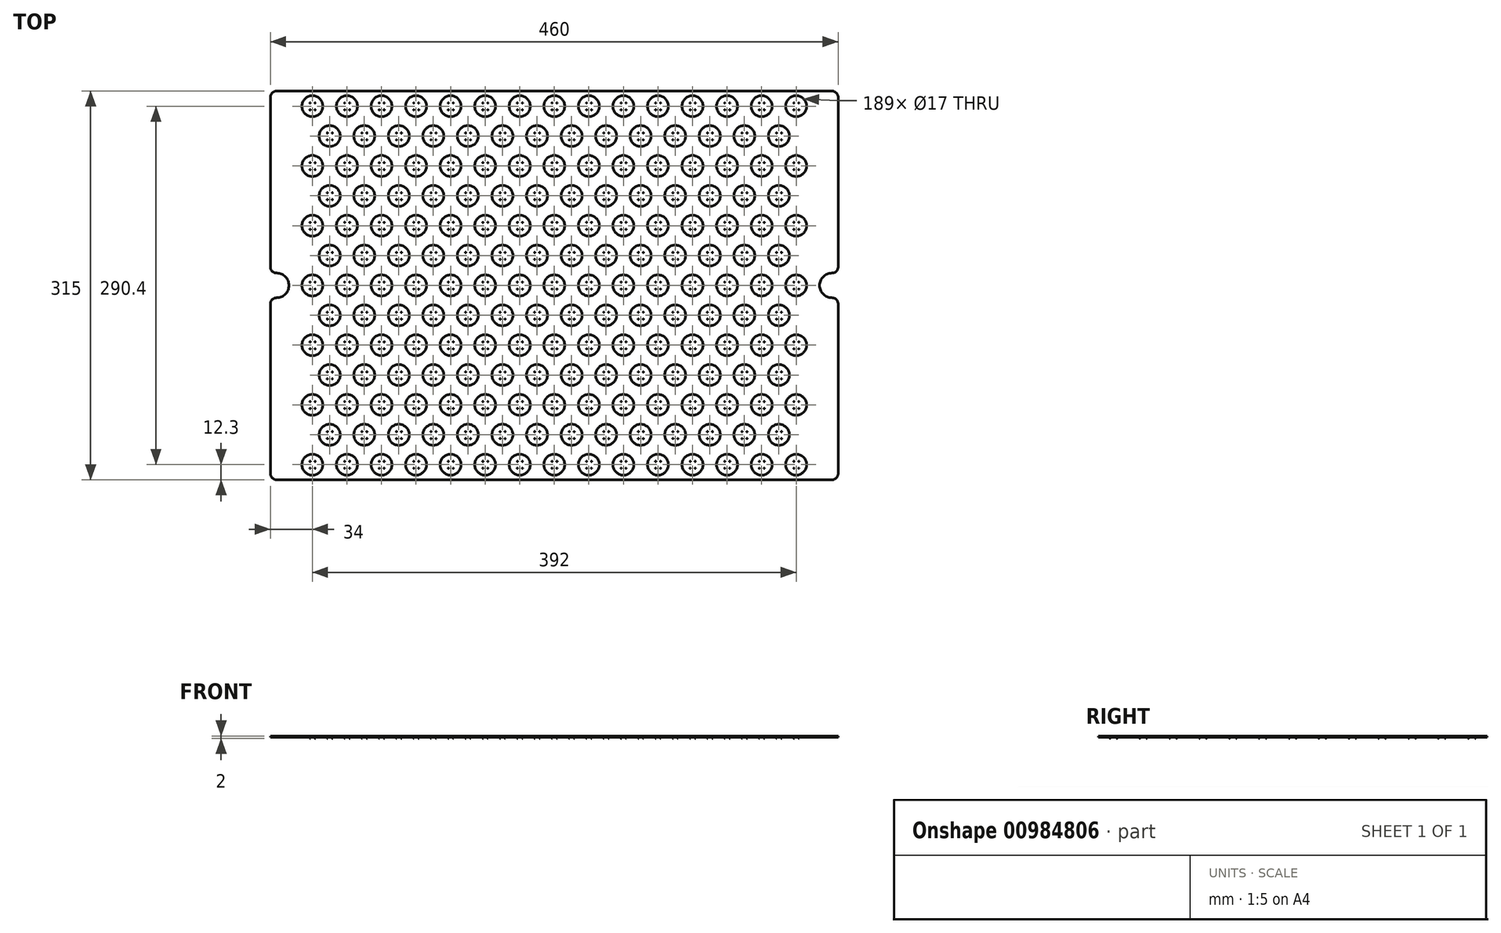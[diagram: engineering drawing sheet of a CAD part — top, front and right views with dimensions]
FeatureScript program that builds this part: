
annotation { "Feature Type Name" : "Feature", "Feature Type Description" : "" }
export const myFeature = defineFeature(function(context is Context, id is Id, definition is map)
    precondition{}
    {
        {
            var Q0;
            Q0=qCreatedBy(makeId("Top.planeOp"),FACE);
            var sketch = newSketch(context, id + "F0", { "sketchPlane" : qUnion([Q0])});
            skLineSegment(sketch, "E0.bottom", {"start": v(-225, 157.5) * mm, "end": v(225, 157.5) * mm});
            skLineSegment(sketch, "E0.top", {"start": v(-225, -157.5) * mm, "end": v(225, -157.5) * mm});
            skLineSegment(sketch, "E0.left", {"start": v(-230, 152.5) * mm, "end": v(-230, 15) * mm});
            skLineSegment(sketch, "E0.right", {"start": v(230, 152.5) * mm, "end": v(230, 15) * mm});
            skPoint(sketch, "E1.visualSharp", {"position": v(-230, 157.5) * mm});
            skArc(sketch, "E1.filletArc", {"start": v(-225, 157.5) * mm, "mid": v(-228.54, 156.04) * mm, "end": v(-230, 152.5) * mm});
            skPoint(sketch, "E2.visualSharp", {"position": v(230, 157.5) * mm});
            skArc(sketch, "E2.filletArc", {"start": v(230, 152.5) * mm, "mid": v(228.54, 156.04) * mm, "end": v(225, 157.5) * mm});
            skPoint(sketch, "E3.visualSharp", {"position": v(230, -157.5) * mm});
            skArc(sketch, "E3.filletArc", {"start": v(225, -157.5) * mm, "mid": v(228.54, -156.04) * mm, "end": v(230, -152.5) * mm});
            skPoint(sketch, "E4.visualSharp", {"position": v(-230, -157.5) * mm});
            skArc(sketch, "E4.filletArc", {"start": v(-230, -152.5) * mm, "mid": v(-228.54, -156.04) * mm, "end": v(-225, -157.5) * mm});
            skArc(sketch, "E5", {"start": v(-225, 10) * mm, "mid": v(-215, 0) * mm, "end": v(-225, -10) * mm});
            skArc(sketch, "E6", {"start": v(225, 10) * mm, "mid": v(215, 0) * mm, "end": v(225, -10) * mm});
            skLineSegment(sketch, "E7.trimOffspring", {"start": v(-230, -15) * mm, "end": v(-230, -152.5) * mm});
            skLineSegment(sketch, "E8.trimOffspring", {"start": v(230, -15) * mm, "end": v(230, -152.5) * mm});
            skPoint(sketch, "E9.visualSharp", {"position": v(230, 8.66) * mm});
            skArc(sketch, "E9.filletArc", {"start": v(225, 10) * mm, "mid": v(228.54, 11.46) * mm, "end": v(230, 15) * mm});
            skPoint(sketch, "E10.visualSharp", {"position": v(230, -8.66) * mm});
            skArc(sketch, "E10.filletArc", {"start": v(230, -15) * mm, "mid": v(228.54, -11.46) * mm, "end": v(225, -10) * mm});
            skPoint(sketch, "E11.visualSharp", {"position": v(-230, 8.66) * mm});
            skArc(sketch, "E11.filletArc", {"start": v(-230, 15) * mm, "mid": v(-228.54, 11.46) * mm, "end": v(-225, 10) * mm});
            skPoint(sketch, "E12.visualSharp", {"position": v(-230, -8.66) * mm});
            skArc(sketch, "E12.filletArc", {"start": v(-225, -10) * mm, "mid": v(-228.54, -11.46) * mm, "end": v(-230, -15) * mm});
            skCircle(sketch, "E13", {"center": v(-196, 145.2) * mm, "radius": 8.5 * mm});
            skCircle(sketch, "E14", {"center": v(-182, 121) * mm, "radius": 8.5 * mm});
            skCircle(sketch, "E15.0.1.0", {"center": v(-196, 96.8) * mm, "radius": 8.5 * mm});
            skCircle(sketch, "E15.0.2.0", {"center": v(-196, 48.4) * mm, "radius": 8.5 * mm});
            skCircle(sketch, "E15.0.3.0", {"center": v(-196, 0) * mm, "radius": 8.5 * mm});
            skCircle(sketch, "E15.0.4.0", {"center": v(-196, -48.4) * mm, "radius": 8.5 * mm});
            skCircle(sketch, "E15.0.5.0", {"center": v(-196, -96.8) * mm, "radius": 8.5 * mm});
            skCircle(sketch, "E15.0.6.0", {"center": v(-196, -145.2) * mm, "radius": 8.5 * mm});
            skCircle(sketch, "E15.1.0.0", {"center": v(-168, 145.2) * mm, "radius": 8.5 * mm});
            skCircle(sketch, "E15.1.1.0", {"center": v(-168, 96.8) * mm, "radius": 8.5 * mm});
            skCircle(sketch, "E15.1.2.0", {"center": v(-168, 48.4) * mm, "radius": 8.5 * mm});
            skCircle(sketch, "E15.1.3.0", {"center": v(-168, 0) * mm, "radius": 8.5 * mm});
            skCircle(sketch, "E15.1.4.0", {"center": v(-168, -48.4) * mm, "radius": 8.5 * mm});
            skCircle(sketch, "E15.1.5.0", {"center": v(-168, -96.8) * mm, "radius": 8.5 * mm});
            skCircle(sketch, "E15.1.6.0", {"center": v(-168, -145.2) * mm, "radius": 8.5 * mm});
            skCircle(sketch, "E15.2.0.0", {"center": v(-140, 145.2) * mm, "radius": 8.5 * mm});
            skCircle(sketch, "E15.2.1.0", {"center": v(-140, 96.8) * mm, "radius": 8.5 * mm});
            skCircle(sketch, "E15.2.2.0", {"center": v(-140, 48.4) * mm, "radius": 8.5 * mm});
            skCircle(sketch, "E15.2.3.0", {"center": v(-140, 0) * mm, "radius": 8.5 * mm});
            skCircle(sketch, "E15.2.4.0", {"center": v(-140, -48.4) * mm, "radius": 8.5 * mm});
            skCircle(sketch, "E15.2.5.0", {"center": v(-140, -96.8) * mm, "radius": 8.5 * mm});
            skCircle(sketch, "E15.2.6.0", {"center": v(-140, -145.2) * mm, "radius": 8.5 * mm});
            skCircle(sketch, "E15.3.0.0", {"center": v(-112, 145.2) * mm, "radius": 8.5 * mm});
            skCircle(sketch, "E15.3.1.0", {"center": v(-112, 96.8) * mm, "radius": 8.5 * mm});
            skCircle(sketch, "E15.3.2.0", {"center": v(-112, 48.4) * mm, "radius": 8.5 * mm});
            skCircle(sketch, "E15.3.3.0", {"center": v(-112, 0) * mm, "radius": 8.5 * mm});
            skCircle(sketch, "E15.3.4.0", {"center": v(-112, -48.4) * mm, "radius": 8.5 * mm});
            skCircle(sketch, "E15.3.5.0", {"center": v(-112, -96.8) * mm, "radius": 8.5 * mm});
            skCircle(sketch, "E15.3.6.0", {"center": v(-112, -145.2) * mm, "radius": 8.5 * mm});
            skCircle(sketch, "E15.4.0.0", {"center": v(-84, 145.2) * mm, "radius": 8.5 * mm});
            skCircle(sketch, "E15.4.1.0", {"center": v(-84, 96.8) * mm, "radius": 8.5 * mm});
            skCircle(sketch, "E15.4.2.0", {"center": v(-84, 48.4) * mm, "radius": 8.5 * mm});
            skCircle(sketch, "E15.4.3.0", {"center": v(-84, 0) * mm, "radius": 8.5 * mm});
            skCircle(sketch, "E15.4.4.0", {"center": v(-84, -48.4) * mm, "radius": 8.5 * mm});
            skCircle(sketch, "E15.4.5.0", {"center": v(-84, -96.8) * mm, "radius": 8.5 * mm});
            skCircle(sketch, "E15.4.6.0", {"center": v(-84, -145.2) * mm, "radius": 8.5 * mm});
            skCircle(sketch, "E15.5.0.0", {"center": v(-56, 145.2) * mm, "radius": 8.5 * mm});
            skCircle(sketch, "E15.5.1.0", {"center": v(-56, 96.8) * mm, "radius": 8.5 * mm});
            skCircle(sketch, "E15.5.2.0", {"center": v(-56, 48.4) * mm, "radius": 8.5 * mm});
            skCircle(sketch, "E15.5.3.0", {"center": v(-56, 0) * mm, "radius": 8.5 * mm});
            skCircle(sketch, "E15.5.4.0", {"center": v(-56, -48.4) * mm, "radius": 8.5 * mm});
            skCircle(sketch, "E15.5.5.0", {"center": v(-56, -96.8) * mm, "radius": 8.5 * mm});
            skCircle(sketch, "E15.5.6.0", {"center": v(-56, -145.2) * mm, "radius": 8.5 * mm});
            skCircle(sketch, "E15.6.0.0", {"center": v(-28, 145.2) * mm, "radius": 8.5 * mm});
            skCircle(sketch, "E15.6.1.0", {"center": v(-28, 96.8) * mm, "radius": 8.5 * mm});
            skCircle(sketch, "E15.6.2.0", {"center": v(-28, 48.4) * mm, "radius": 8.5 * mm});
            skCircle(sketch, "E15.6.3.0", {"center": v(-28, 0) * mm, "radius": 8.5 * mm});
            skCircle(sketch, "E15.6.4.0", {"center": v(-28, -48.4) * mm, "radius": 8.5 * mm});
            skCircle(sketch, "E15.6.5.0", {"center": v(-28, -96.8) * mm, "radius": 8.5 * mm});
            skCircle(sketch, "E15.6.6.0", {"center": v(-28, -145.2) * mm, "radius": 8.5 * mm});
            skCircle(sketch, "E15.7.0.0", {"center": v(0, 145.2) * mm, "radius": 8.5 * mm});
            skCircle(sketch, "E15.7.1.0", {"center": v(0, 96.8) * mm, "radius": 8.5 * mm});
            skCircle(sketch, "E15.7.2.0", {"center": v(0, 48.4) * mm, "radius": 8.5 * mm});
            skCircle(sketch, "E15.7.3.0", {"center": v(0, 0) * mm, "radius": 8.5 * mm});
            skCircle(sketch, "E15.7.4.0", {"center": v(0, -48.4) * mm, "radius": 8.5 * mm});
            skCircle(sketch, "E15.7.5.0", {"center": v(0, -96.8) * mm, "radius": 8.5 * mm});
            skCircle(sketch, "E15.7.6.0", {"center": v(0, -145.2) * mm, "radius": 8.5 * mm});
            skCircle(sketch, "E15.8.0.0", {"center": v(28, 145.2) * mm, "radius": 8.5 * mm});
            skCircle(sketch, "E15.8.1.0", {"center": v(28, 96.8) * mm, "radius": 8.5 * mm});
            skCircle(sketch, "E15.8.2.0", {"center": v(28, 48.4) * mm, "radius": 8.5 * mm});
            skCircle(sketch, "E15.8.3.0", {"center": v(28, 0) * mm, "radius": 8.5 * mm});
            skCircle(sketch, "E15.8.4.0", {"center": v(28, -48.4) * mm, "radius": 8.5 * mm});
            skCircle(sketch, "E15.8.5.0", {"center": v(28, -96.8) * mm, "radius": 8.5 * mm});
            skCircle(sketch, "E15.8.6.0", {"center": v(28, -145.2) * mm, "radius": 8.5 * mm});
            skCircle(sketch, "E15.9.0.0", {"center": v(56, 145.2) * mm, "radius": 8.5 * mm});
            skCircle(sketch, "E15.9.1.0", {"center": v(56, 96.8) * mm, "radius": 8.5 * mm});
            skCircle(sketch, "E15.9.2.0", {"center": v(56, 48.4) * mm, "radius": 8.5 * mm});
            skCircle(sketch, "E15.9.3.0", {"center": v(56, 0) * mm, "radius": 8.5 * mm});
            skCircle(sketch, "E15.9.4.0", {"center": v(56, -48.4) * mm, "radius": 8.5 * mm});
            skCircle(sketch, "E15.9.5.0", {"center": v(56, -96.8) * mm, "radius": 8.5 * mm});
            skCircle(sketch, "E15.9.6.0", {"center": v(56, -145.2) * mm, "radius": 8.5 * mm});
            skCircle(sketch, "E15.10.0.0", {"center": v(84, 145.2) * mm, "radius": 8.5 * mm});
            skCircle(sketch, "E15.10.1.0", {"center": v(84, 96.8) * mm, "radius": 8.5 * mm});
            skCircle(sketch, "E15.10.2.0", {"center": v(84, 48.4) * mm, "radius": 8.5 * mm});
            skCircle(sketch, "E15.10.3.0", {"center": v(84, 0) * mm, "radius": 8.5 * mm});
            skCircle(sketch, "E15.10.4.0", {"center": v(84, -48.4) * mm, "radius": 8.5 * mm});
            skCircle(sketch, "E15.10.5.0", {"center": v(84, -96.8) * mm, "radius": 8.5 * mm});
            skCircle(sketch, "E15.10.6.0", {"center": v(84, -145.2) * mm, "radius": 8.5 * mm});
            skCircle(sketch, "E15.11.0.0", {"center": v(112, 145.2) * mm, "radius": 8.5 * mm});
            skCircle(sketch, "E15.11.1.0", {"center": v(112, 96.8) * mm, "radius": 8.5 * mm});
            skCircle(sketch, "E15.11.2.0", {"center": v(112, 48.4) * mm, "radius": 8.5 * mm});
            skCircle(sketch, "E15.11.3.0", {"center": v(112, 0) * mm, "radius": 8.5 * mm});
            skCircle(sketch, "E15.11.4.0", {"center": v(112, -48.4) * mm, "radius": 8.5 * mm});
            skCircle(sketch, "E15.11.5.0", {"center": v(112, -96.8) * mm, "radius": 8.5 * mm});
            skCircle(sketch, "E15.11.6.0", {"center": v(112, -145.2) * mm, "radius": 8.5 * mm});
            skCircle(sketch, "E15.12.0.0", {"center": v(140, 145.2) * mm, "radius": 8.5 * mm});
            skCircle(sketch, "E15.12.1.0", {"center": v(140, 96.8) * mm, "radius": 8.5 * mm});
            skCircle(sketch, "E15.12.2.0", {"center": v(140, 48.4) * mm, "radius": 8.5 * mm});
            skCircle(sketch, "E15.12.3.0", {"center": v(140, 0) * mm, "radius": 8.5 * mm});
            skCircle(sketch, "E15.12.4.0", {"center": v(140, -48.4) * mm, "radius": 8.5 * mm});
            skCircle(sketch, "E15.12.5.0", {"center": v(140, -96.8) * mm, "radius": 8.5 * mm});
            skCircle(sketch, "E15.12.6.0", {"center": v(140, -145.2) * mm, "radius": 8.5 * mm});
            skCircle(sketch, "E15.13.0.0", {"center": v(168, 145.2) * mm, "radius": 8.5 * mm});
            skCircle(sketch, "E15.13.1.0", {"center": v(168, 96.8) * mm, "radius": 8.5 * mm});
            skCircle(sketch, "E15.13.2.0", {"center": v(168, 48.4) * mm, "radius": 8.5 * mm});
            skCircle(sketch, "E15.13.3.0", {"center": v(168, 0) * mm, "radius": 8.5 * mm});
            skCircle(sketch, "E15.13.4.0", {"center": v(168, -48.4) * mm, "radius": 8.5 * mm});
            skCircle(sketch, "E15.13.5.0", {"center": v(168, -96.8) * mm, "radius": 8.5 * mm});
            skCircle(sketch, "E15.13.6.0", {"center": v(168, -145.2) * mm, "radius": 8.5 * mm});
            skCircle(sketch, "E15.14.0.0", {"center": v(196, 145.2) * mm, "radius": 8.5 * mm});
            skCircle(sketch, "E15.14.1.0", {"center": v(196, 96.8) * mm, "radius": 8.5 * mm});
            skCircle(sketch, "E15.14.2.0", {"center": v(196, 48.4) * mm, "radius": 8.5 * mm});
            skCircle(sketch, "E15.14.3.0", {"center": v(196, 0) * mm, "radius": 8.5 * mm});
            skCircle(sketch, "E15.14.4.0", {"center": v(196, -48.4) * mm, "radius": 8.5 * mm});
            skCircle(sketch, "E15.14.5.0", {"center": v(196, -96.8) * mm, "radius": 8.5 * mm});
            skCircle(sketch, "E15.14.6.0", {"center": v(196, -145.2) * mm, "radius": 8.5 * mm});
            skLineSegment(sketch, "E15.direction1", {"start": v(-196, 145.2) * mm, "end": v(-168, 145.2) * mm, "construction": true});
            skLineSegment(sketch, "E15.direction2", {"start": v(-196, 145.2) * mm, "end": v(-196, 96.8) * mm, "construction": true});
            skCircle(sketch, "E16.0.1.0", {"center": v(-182, 72.6) * mm, "radius": 8.5 * mm});
            skCircle(sketch, "E16.0.2.0", {"center": v(-182, 24.2) * mm, "radius": 8.5 * mm});
            skCircle(sketch, "E16.0.3.0", {"center": v(-182, -24.2) * mm, "radius": 8.5 * mm});
            skCircle(sketch, "E16.0.4.0", {"center": v(-182, -72.6) * mm, "radius": 8.5 * mm});
            skCircle(sketch, "E16.0.5.0", {"center": v(-182, -121) * mm, "radius": 8.5 * mm});
            skCircle(sketch, "E16.1.0.0", {"center": v(-154, 121) * mm, "radius": 8.5 * mm});
            skCircle(sketch, "E16.1.1.0", {"center": v(-154, 72.6) * mm, "radius": 8.5 * mm});
            skCircle(sketch, "E16.1.2.0", {"center": v(-154, 24.2) * mm, "radius": 8.5 * mm});
            skCircle(sketch, "E16.1.3.0", {"center": v(-154, -24.2) * mm, "radius": 8.5 * mm});
            skCircle(sketch, "E16.1.4.0", {"center": v(-154, -72.6) * mm, "radius": 8.5 * mm});
            skCircle(sketch, "E16.1.5.0", {"center": v(-154, -121) * mm, "radius": 8.5 * mm});
            skCircle(sketch, "E16.2.0.0", {"center": v(-126, 121) * mm, "radius": 8.5 * mm});
            skCircle(sketch, "E16.2.1.0", {"center": v(-126, 72.6) * mm, "radius": 8.5 * mm});
            skCircle(sketch, "E16.2.2.0", {"center": v(-126, 24.2) * mm, "radius": 8.5 * mm});
            skCircle(sketch, "E16.2.3.0", {"center": v(-126, -24.2) * mm, "radius": 8.5 * mm});
            skCircle(sketch, "E16.2.4.0", {"center": v(-126, -72.6) * mm, "radius": 8.5 * mm});
            skCircle(sketch, "E16.2.5.0", {"center": v(-126, -121) * mm, "radius": 8.5 * mm});
            skCircle(sketch, "E16.3.0.0", {"center": v(-98, 121) * mm, "radius": 8.5 * mm});
            skCircle(sketch, "E16.3.1.0", {"center": v(-98, 72.6) * mm, "radius": 8.5 * mm});
            skCircle(sketch, "E16.3.2.0", {"center": v(-98, 24.2) * mm, "radius": 8.5 * mm});
            skCircle(sketch, "E16.3.3.0", {"center": v(-98, -24.2) * mm, "radius": 8.5 * mm});
            skCircle(sketch, "E16.3.4.0", {"center": v(-98, -72.6) * mm, "radius": 8.5 * mm});
            skCircle(sketch, "E16.3.5.0", {"center": v(-98, -121) * mm, "radius": 8.5 * mm});
            skCircle(sketch, "E16.4.0.0", {"center": v(-70, 121) * mm, "radius": 8.5 * mm});
            skCircle(sketch, "E16.4.1.0", {"center": v(-70, 72.6) * mm, "radius": 8.5 * mm});
            skCircle(sketch, "E16.4.2.0", {"center": v(-70, 24.2) * mm, "radius": 8.5 * mm});
            skCircle(sketch, "E16.4.3.0", {"center": v(-70, -24.2) * mm, "radius": 8.5 * mm});
            skCircle(sketch, "E16.4.4.0", {"center": v(-70, -72.6) * mm, "radius": 8.5 * mm});
            skCircle(sketch, "E16.4.5.0", {"center": v(-70, -121) * mm, "radius": 8.5 * mm});
            skCircle(sketch, "E16.5.0.0", {"center": v(-42, 121) * mm, "radius": 8.5 * mm});
            skCircle(sketch, "E16.5.1.0", {"center": v(-42, 72.6) * mm, "radius": 8.5 * mm});
            skCircle(sketch, "E16.5.2.0", {"center": v(-42, 24.2) * mm, "radius": 8.5 * mm});
            skCircle(sketch, "E16.5.3.0", {"center": v(-42, -24.2) * mm, "radius": 8.5 * mm});
            skCircle(sketch, "E16.5.4.0", {"center": v(-42, -72.6) * mm, "radius": 8.5 * mm});
            skCircle(sketch, "E16.5.5.0", {"center": v(-42, -121) * mm, "radius": 8.5 * mm});
            skCircle(sketch, "E16.6.0.0", {"center": v(-14, 121) * mm, "radius": 8.5 * mm});
            skCircle(sketch, "E16.6.1.0", {"center": v(-14, 72.6) * mm, "radius": 8.5 * mm});
            skCircle(sketch, "E16.6.2.0", {"center": v(-14, 24.2) * mm, "radius": 8.5 * mm});
            skCircle(sketch, "E16.6.3.0", {"center": v(-14, -24.2) * mm, "radius": 8.5 * mm});
            skCircle(sketch, "E16.6.4.0", {"center": v(-14, -72.6) * mm, "radius": 8.5 * mm});
            skCircle(sketch, "E16.6.5.0", {"center": v(-14, -121) * mm, "radius": 8.5 * mm});
            skCircle(sketch, "E16.7.0.0", {"center": v(14, 121) * mm, "radius": 8.5 * mm});
            skCircle(sketch, "E16.7.1.0", {"center": v(14, 72.6) * mm, "radius": 8.5 * mm});
            skCircle(sketch, "E16.7.2.0", {"center": v(14, 24.2) * mm, "radius": 8.5 * mm});
            skCircle(sketch, "E16.7.3.0", {"center": v(14, -24.2) * mm, "radius": 8.5 * mm});
            skCircle(sketch, "E16.7.4.0", {"center": v(14, -72.6) * mm, "radius": 8.5 * mm});
            skCircle(sketch, "E16.7.5.0", {"center": v(14, -121) * mm, "radius": 8.5 * mm});
            skCircle(sketch, "E16.8.0.0", {"center": v(42, 121) * mm, "radius": 8.5 * mm});
            skCircle(sketch, "E16.8.1.0", {"center": v(42, 72.6) * mm, "radius": 8.5 * mm});
            skCircle(sketch, "E16.8.2.0", {"center": v(42, 24.2) * mm, "radius": 8.5 * mm});
            skCircle(sketch, "E16.8.3.0", {"center": v(42, -24.2) * mm, "radius": 8.5 * mm});
            skCircle(sketch, "E16.8.4.0", {"center": v(42, -72.6) * mm, "radius": 8.5 * mm});
            skCircle(sketch, "E16.8.5.0", {"center": v(42, -121) * mm, "radius": 8.5 * mm});
            skCircle(sketch, "E16.9.0.0", {"center": v(70, 121) * mm, "radius": 8.5 * mm});
            skCircle(sketch, "E16.9.1.0", {"center": v(70, 72.6) * mm, "radius": 8.5 * mm});
            skCircle(sketch, "E16.9.2.0", {"center": v(70, 24.2) * mm, "radius": 8.5 * mm});
            skCircle(sketch, "E16.9.3.0", {"center": v(70, -24.2) * mm, "radius": 8.5 * mm});
            skCircle(sketch, "E16.9.4.0", {"center": v(70, -72.6) * mm, "radius": 8.5 * mm});
            skCircle(sketch, "E16.9.5.0", {"center": v(70, -121) * mm, "radius": 8.5 * mm});
            skCircle(sketch, "E16.10.0.0", {"center": v(98, 121) * mm, "radius": 8.5 * mm});
            skCircle(sketch, "E16.10.1.0", {"center": v(98, 72.6) * mm, "radius": 8.5 * mm});
            skCircle(sketch, "E16.10.2.0", {"center": v(98, 24.2) * mm, "radius": 8.5 * mm});
            skCircle(sketch, "E16.10.3.0", {"center": v(98, -24.2) * mm, "radius": 8.5 * mm});
            skCircle(sketch, "E16.10.4.0", {"center": v(98, -72.6) * mm, "radius": 8.5 * mm});
            skCircle(sketch, "E16.10.5.0", {"center": v(98, -121) * mm, "radius": 8.5 * mm});
            skCircle(sketch, "E16.11.0.0", {"center": v(126, 121) * mm, "radius": 8.5 * mm});
            skCircle(sketch, "E16.11.1.0", {"center": v(126, 72.6) * mm, "radius": 8.5 * mm});
            skCircle(sketch, "E16.11.2.0", {"center": v(126, 24.2) * mm, "radius": 8.5 * mm});
            skCircle(sketch, "E16.11.3.0", {"center": v(126, -24.2) * mm, "radius": 8.5 * mm});
            skCircle(sketch, "E16.11.4.0", {"center": v(126, -72.6) * mm, "radius": 8.5 * mm});
            skCircle(sketch, "E16.11.5.0", {"center": v(126, -121) * mm, "radius": 8.5 * mm});
            skCircle(sketch, "E16.12.0.0", {"center": v(154, 121) * mm, "radius": 8.5 * mm});
            skCircle(sketch, "E16.12.1.0", {"center": v(154, 72.6) * mm, "radius": 8.5 * mm});
            skCircle(sketch, "E16.12.2.0", {"center": v(154, 24.2) * mm, "radius": 8.5 * mm});
            skCircle(sketch, "E16.12.3.0", {"center": v(154, -24.2) * mm, "radius": 8.5 * mm});
            skCircle(sketch, "E16.12.4.0", {"center": v(154, -72.6) * mm, "radius": 8.5 * mm});
            skCircle(sketch, "E16.12.5.0", {"center": v(154, -121) * mm, "radius": 8.5 * mm});
            skCircle(sketch, "E16.13.0.0", {"center": v(182, 121) * mm, "radius": 8.5 * mm});
            skCircle(sketch, "E16.13.1.0", {"center": v(182, 72.6) * mm, "radius": 8.5 * mm});
            skCircle(sketch, "E16.13.2.0", {"center": v(182, 24.2) * mm, "radius": 8.5 * mm});
            skCircle(sketch, "E16.13.3.0", {"center": v(182, -24.2) * mm, "radius": 8.5 * mm});
            skCircle(sketch, "E16.13.4.0", {"center": v(182, -72.6) * mm, "radius": 8.5 * mm});
            skCircle(sketch, "E16.13.5.0", {"center": v(182, -121) * mm, "radius": 8.5 * mm});
            skLineSegment(sketch, "E16.direction1", {"start": v(-182, 121) * mm, "end": v(-154, 121) * mm, "construction": true});
            skLineSegment(sketch, "E16.direction2", {"start": v(-182, 121) * mm, "end": v(-182, 72.6) * mm, "construction": true});
            skSolve(sketch);
        }
        {
            var Q0;
            Q0=makeQuery(id+"F0.imprint","IMPRINT",FACE,{"disambiguationData":[TD([[makeQuery(id+"F0.imprint","IMPRINT",EDGE,{"derivedFrom":sQuery(id+"F0.wireOp",EDGE,"E0.bottom")}),-1.0]])]});
            extrude(context, id + "F1", {"entities" : qUnion([Q0]), "depth" : 1 * mm, "offsetDistance" : 25 * mm});
        }
        {
            var Q0;
            Q0=makeQuery(id+"F1.opExtrude","CAP_FACE",FACE,{"disambiguationData":[OSD([sQuery(id+"F0.wireOp",EDGE,"E0.bottom"),sQuery(id+"F0.wireOp",EDGE,"E0.top"),sQuery(id+"F0.wireOp",EDGE,"E0.left"),sQuery(id+"F0.wireOp",EDGE,"E0.right"),sQuery(id+"F0.wireOp",EDGE,"E1.filletArc"),sQuery(id+"F0.wireOp",EDGE,"E2.filletArc"),sQuery(id+"F0.wireOp",EDGE,"E3.filletArc"),sQuery(id+"F0.wireOp",EDGE,"E4.filletArc"),sQuery(id+"F0.wireOp",EDGE,"E5"),sQuery(id+"F0.wireOp",EDGE,"E6"),sQuery(id+"F0.wireOp",EDGE,"E7.trimOffspring"),sQuery(id+"F0.wireOp",EDGE,"E8.trimOffspring"),sQuery(id+"F0.wireOp",EDGE,"E9.filletArc"),sQuery(id+"F0.wireOp",EDGE,"E10.filletArc"),sQuery(id+"F0.wireOp",EDGE,"E11.filletArc"),sQuery(id+"F0.wireOp",EDGE,"E12.filletArc"),sQuery(id+"F0.wireOp",EDGE,"E13"),sQuery(id+"F0.wireOp",EDGE,"E14"),sQuery(id+"F0.wireOp",EDGE,"E15.0.1.0"),sQuery(id+"F0.wireOp",EDGE,"E15.0.2.0"),sQuery(id+"F0.wireOp",EDGE,"E15.0.3.0"),sQuery(id+"F0.wireOp",EDGE,"E15.0.4.0"),sQuery(id+"F0.wireOp",EDGE,"E15.0.5.0"),sQuery(id+"F0.wireOp",EDGE,"E15.0.6.0"),sQuery(id+"F0.wireOp",EDGE,"E15.1.0.0"),sQuery(id+"F0.wireOp",EDGE,"E15.1.1.0"),sQuery(id+"F0.wireOp",EDGE,"E15.1.2.0"),sQuery(id+"F0.wireOp",EDGE,"E15.1.3.0"),sQuery(id+"F0.wireOp",EDGE,"E15.1.4.0"),sQuery(id+"F0.wireOp",EDGE,"E15.1.5.0"),sQuery(id+"F0.wireOp",EDGE,"E15.1.6.0"),sQuery(id+"F0.wireOp",EDGE,"E15.2.0.0"),sQuery(id+"F0.wireOp",EDGE,"E15.2.1.0"),sQuery(id+"F0.wireOp",EDGE,"E15.2.2.0"),sQuery(id+"F0.wireOp",EDGE,"E15.2.3.0"),sQuery(id+"F0.wireOp",EDGE,"E15.2.4.0"),sQuery(id+"F0.wireOp",EDGE,"E15.2.5.0"),sQuery(id+"F0.wireOp",EDGE,"E15.2.6.0"),sQuery(id+"F0.wireOp",EDGE,"E15.3.0.0"),sQuery(id+"F0.wireOp",EDGE,"E15.3.1.0"),sQuery(id+"F0.wireOp",EDGE,"E15.3.2.0"),sQuery(id+"F0.wireOp",EDGE,"E15.3.3.0"),sQuery(id+"F0.wireOp",EDGE,"E15.3.4.0"),sQuery(id+"F0.wireOp",EDGE,"E15.3.5.0"),sQuery(id+"F0.wireOp",EDGE,"E15.3.6.0"),sQuery(id+"F0.wireOp",EDGE,"E15.4.0.0"),sQuery(id+"F0.wireOp",EDGE,"E15.4.1.0"),sQuery(id+"F0.wireOp",EDGE,"E15.4.2.0"),sQuery(id+"F0.wireOp",EDGE,"E15.4.3.0"),sQuery(id+"F0.wireOp",EDGE,"E15.4.4.0"),sQuery(id+"F0.wireOp",EDGE,"E15.4.5.0"),sQuery(id+"F0.wireOp",EDGE,"E15.4.6.0"),sQuery(id+"F0.wireOp",EDGE,"E15.5.0.0"),sQuery(id+"F0.wireOp",EDGE,"E15.5.1.0"),sQuery(id+"F0.wireOp",EDGE,"E15.5.2.0"),sQuery(id+"F0.wireOp",EDGE,"E15.5.3.0"),sQuery(id+"F0.wireOp",EDGE,"E15.5.4.0"),sQuery(id+"F0.wireOp",EDGE,"E15.5.5.0"),sQuery(id+"F0.wireOp",EDGE,"E15.5.6.0"),sQuery(id+"F0.wireOp",EDGE,"E15.6.0.0"),sQuery(id+"F0.wireOp",EDGE,"E15.6.1.0"),sQuery(id+"F0.wireOp",EDGE,"E15.6.2.0"),sQuery(id+"F0.wireOp",EDGE,"E15.6.3.0"),sQuery(id+"F0.wireOp",EDGE,"E15.6.4.0"),sQuery(id+"F0.wireOp",EDGE,"E15.6.5.0"),sQuery(id+"F0.wireOp",EDGE,"E15.6.6.0"),sQuery(id+"F0.wireOp",EDGE,"E15.7.0.0"),sQuery(id+"F0.wireOp",EDGE,"E15.7.1.0"),sQuery(id+"F0.wireOp",EDGE,"E15.7.2.0"),sQuery(id+"F0.wireOp",EDGE,"E15.7.3.0"),sQuery(id+"F0.wireOp",EDGE,"E15.7.4.0"),sQuery(id+"F0.wireOp",EDGE,"E15.7.5.0"),sQuery(id+"F0.wireOp",EDGE,"E15.7.6.0"),sQuery(id+"F0.wireOp",EDGE,"E15.8.0.0"),sQuery(id+"F0.wireOp",EDGE,"E15.8.1.0"),sQuery(id+"F0.wireOp",EDGE,"E15.8.2.0"),sQuery(id+"F0.wireOp",EDGE,"E15.8.3.0"),sQuery(id+"F0.wireOp",EDGE,"E15.8.4.0"),sQuery(id+"F0.wireOp",EDGE,"E15.8.5.0"),sQuery(id+"F0.wireOp",EDGE,"E15.8.6.0"),sQuery(id+"F0.wireOp",EDGE,"E15.9.0.0"),sQuery(id+"F0.wireOp",EDGE,"E15.9.1.0"),sQuery(id+"F0.wireOp",EDGE,"E15.9.2.0"),sQuery(id+"F0.wireOp",EDGE,"E15.9.3.0"),sQuery(id+"F0.wireOp",EDGE,"E15.9.4.0"),sQuery(id+"F0.wireOp",EDGE,"E15.9.5.0"),sQuery(id+"F0.wireOp",EDGE,"E15.9.6.0"),sQuery(id+"F0.wireOp",EDGE,"E15.10.0.0"),sQuery(id+"F0.wireOp",EDGE,"E15.10.1.0"),sQuery(id+"F0.wireOp",EDGE,"E15.10.2.0"),sQuery(id+"F0.wireOp",EDGE,"E15.10.3.0"),sQuery(id+"F0.wireOp",EDGE,"E15.10.4.0"),sQuery(id+"F0.wireOp",EDGE,"E15.10.5.0"),sQuery(id+"F0.wireOp",EDGE,"E15.10.6.0"),sQuery(id+"F0.wireOp",EDGE,"E15.11.0.0"),sQuery(id+"F0.wireOp",EDGE,"E15.11.1.0"),sQuery(id+"F0.wireOp",EDGE,"E15.11.2.0"),sQuery(id+"F0.wireOp",EDGE,"E15.11.3.0"),sQuery(id+"F0.wireOp",EDGE,"E15.11.4.0"),sQuery(id+"F0.wireOp",EDGE,"E15.11.5.0"),sQuery(id+"F0.wireOp",EDGE,"E15.11.6.0"),sQuery(id+"F0.wireOp",EDGE,"E15.12.0.0"),sQuery(id+"F0.wireOp",EDGE,"E15.12.1.0"),sQuery(id+"F0.wireOp",EDGE,"E15.12.2.0"),sQuery(id+"F0.wireOp",EDGE,"E15.12.3.0"),sQuery(id+"F0.wireOp",EDGE,"E15.12.4.0"),sQuery(id+"F0.wireOp",EDGE,"E15.12.5.0"),sQuery(id+"F0.wireOp",EDGE,"E15.12.6.0"),sQuery(id+"F0.wireOp",EDGE,"E15.13.0.0"),sQuery(id+"F0.wireOp",EDGE,"E15.13.1.0"),sQuery(id+"F0.wireOp",EDGE,"E15.13.2.0"),sQuery(id+"F0.wireOp",EDGE,"E15.13.3.0"),sQuery(id+"F0.wireOp",EDGE,"E15.13.4.0"),sQuery(id+"F0.wireOp",EDGE,"E15.13.5.0"),sQuery(id+"F0.wireOp",EDGE,"E15.13.6.0"),sQuery(id+"F0.wireOp",EDGE,"E15.14.0.0"),sQuery(id+"F0.wireOp",EDGE,"E15.14.1.0"),sQuery(id+"F0.wireOp",EDGE,"E15.14.2.0"),sQuery(id+"F0.wireOp",EDGE,"E15.14.3.0"),sQuery(id+"F0.wireOp",EDGE,"E15.14.4.0"),sQuery(id+"F0.wireOp",EDGE,"E15.14.5.0"),sQuery(id+"F0.wireOp",EDGE,"E15.14.6.0"),sQuery(id+"F0.wireOp",EDGE,"E16.0.1.0"),sQuery(id+"F0.wireOp",EDGE,"E16.0.2.0"),sQuery(id+"F0.wireOp",EDGE,"E16.0.3.0"),sQuery(id+"F0.wireOp",EDGE,"E16.0.4.0"),sQuery(id+"F0.wireOp",EDGE,"E16.0.5.0"),sQuery(id+"F0.wireOp",EDGE,"E16.1.0.0"),sQuery(id+"F0.wireOp",EDGE,"E16.1.1.0"),sQuery(id+"F0.wireOp",EDGE,"E16.1.2.0"),sQuery(id+"F0.wireOp",EDGE,"E16.1.3.0"),sQuery(id+"F0.wireOp",EDGE,"E16.1.4.0"),sQuery(id+"F0.wireOp",EDGE,"E16.1.5.0"),sQuery(id+"F0.wireOp",EDGE,"E16.2.0.0"),sQuery(id+"F0.wireOp",EDGE,"E16.2.1.0"),sQuery(id+"F0.wireOp",EDGE,"E16.2.2.0"),sQuery(id+"F0.wireOp",EDGE,"E16.2.3.0"),sQuery(id+"F0.wireOp",EDGE,"E16.2.4.0"),sQuery(id+"F0.wireOp",EDGE,"E16.2.5.0"),sQuery(id+"F0.wireOp",EDGE,"E16.3.0.0"),sQuery(id+"F0.wireOp",EDGE,"E16.3.1.0"),sQuery(id+"F0.wireOp",EDGE,"E16.3.2.0"),sQuery(id+"F0.wireOp",EDGE,"E16.3.3.0"),sQuery(id+"F0.wireOp",EDGE,"E16.3.4.0"),sQuery(id+"F0.wireOp",EDGE,"E16.3.5.0"),sQuery(id+"F0.wireOp",EDGE,"E16.4.0.0"),sQuery(id+"F0.wireOp",EDGE,"E16.4.1.0"),sQuery(id+"F0.wireOp",EDGE,"E16.4.2.0"),sQuery(id+"F0.wireOp",EDGE,"E16.4.3.0"),sQuery(id+"F0.wireOp",EDGE,"E16.4.4.0"),sQuery(id+"F0.wireOp",EDGE,"E16.4.5.0"),sQuery(id+"F0.wireOp",EDGE,"E16.5.0.0"),sQuery(id+"F0.wireOp",EDGE,"E16.5.1.0"),sQuery(id+"F0.wireOp",EDGE,"E16.5.2.0"),sQuery(id+"F0.wireOp",EDGE,"E16.5.3.0"),sQuery(id+"F0.wireOp",EDGE,"E16.5.4.0"),sQuery(id+"F0.wireOp",EDGE,"E16.5.5.0"),sQuery(id+"F0.wireOp",EDGE,"E16.6.0.0"),sQuery(id+"F0.wireOp",EDGE,"E16.6.1.0"),sQuery(id+"F0.wireOp",EDGE,"E16.6.2.0"),sQuery(id+"F0.wireOp",EDGE,"E16.6.3.0"),sQuery(id+"F0.wireOp",EDGE,"E16.6.4.0"),sQuery(id+"F0.wireOp",EDGE,"E16.6.5.0"),sQuery(id+"F0.wireOp",EDGE,"E16.7.0.0"),sQuery(id+"F0.wireOp",EDGE,"E16.7.1.0"),sQuery(id+"F0.wireOp",EDGE,"E16.7.2.0"),sQuery(id+"F0.wireOp",EDGE,"E16.7.3.0"),sQuery(id+"F0.wireOp",EDGE,"E16.7.4.0"),sQuery(id+"F0.wireOp",EDGE,"E16.7.5.0"),sQuery(id+"F0.wireOp",EDGE,"E16.8.0.0"),sQuery(id+"F0.wireOp",EDGE,"E16.8.1.0"),sQuery(id+"F0.wireOp",EDGE,"E16.8.2.0"),sQuery(id+"F0.wireOp",EDGE,"E16.8.3.0"),sQuery(id+"F0.wireOp",EDGE,"E16.8.4.0"),sQuery(id+"F0.wireOp",EDGE,"E16.8.5.0"),sQuery(id+"F0.wireOp",EDGE,"E16.9.0.0"),sQuery(id+"F0.wireOp",EDGE,"E16.9.1.0"),sQuery(id+"F0.wireOp",EDGE,"E16.9.2.0"),sQuery(id+"F0.wireOp",EDGE,"E16.9.3.0"),sQuery(id+"F0.wireOp",EDGE,"E16.9.4.0"),sQuery(id+"F0.wireOp",EDGE,"E16.9.5.0"),sQuery(id+"F0.wireOp",EDGE,"E16.10.0.0"),sQuery(id+"F0.wireOp",EDGE,"E16.10.1.0"),sQuery(id+"F0.wireOp",EDGE,"E16.10.2.0"),sQuery(id+"F0.wireOp",EDGE,"E16.10.3.0"),sQuery(id+"F0.wireOp",EDGE,"E16.10.4.0"),sQuery(id+"F0.wireOp",EDGE,"E16.10.5.0"),sQuery(id+"F0.wireOp",EDGE,"E16.11.0.0"),sQuery(id+"F0.wireOp",EDGE,"E16.11.1.0"),sQuery(id+"F0.wireOp",EDGE,"E16.11.2.0"),sQuery(id+"F0.wireOp",EDGE,"E16.11.3.0"),sQuery(id+"F0.wireOp",EDGE,"E16.11.4.0"),sQuery(id+"F0.wireOp",EDGE,"E16.11.5.0"),sQuery(id+"F0.wireOp",EDGE,"E16.12.0.0"),sQuery(id+"F0.wireOp",EDGE,"E16.12.1.0"),sQuery(id+"F0.wireOp",EDGE,"E16.12.2.0"),sQuery(id+"F0.wireOp",EDGE,"E16.12.3.0"),sQuery(id+"F0.wireOp",EDGE,"E16.12.4.0"),sQuery(id+"F0.wireOp",EDGE,"E16.12.5.0"),sQuery(id+"F0.wireOp",EDGE,"E16.13.0.0"),sQuery(id+"F0.wireOp",EDGE,"E16.13.1.0"),sQuery(id+"F0.wireOp",EDGE,"E16.13.2.0"),sQuery(id+"F0.wireOp",EDGE,"E16.13.3.0"),sQuery(id+"F0.wireOp",EDGE,"E16.13.4.0"),sQuery(id+"F0.wireOp",EDGE,"E16.13.5.0")])],"isStart":true});
            var sketch = newSketch(context, id + "F2", { "sketchPlane" : qUnion([Q0])});
            skCircle(sketch, "E17", {"center": v(-197.83, -147.84) * mm, "radius": 0.25 * mm});
            skCircle(sketch, "E18", {"center": v(-193.83, -147.84) * mm, "radius": 0.25 * mm});
            skCircle(sketch, "E19", {"center": v(-197.83, -142.24) * mm, "radius": 0.25 * mm});
            skCircle(sketch, "E20", {"center": v(-193.83, -142.24) * mm, "radius": 0.25 * mm});
            skCircle(sketch, "E21", {"center": v(-183.85, -123.5) * mm, "radius": 0.25 * mm});
            skCircle(sketch, "E22", {"center": v(-179.85, -123.5) * mm, "radius": 0.25 * mm});
            skCircle(sketch, "E23", {"center": v(-179.85, -117.9) * mm, "radius": 0.25 * mm});
            skCircle(sketch, "E24", {"center": v(-183.85, -117.9) * mm, "radius": 0.25 * mm});
            skCircle(sketch, "E25.0.1.0", {"center": v(-197.83, -99.44) * mm, "radius": 0.25 * mm});
            skCircle(sketch, "E25.0.1.1", {"center": v(-193.83, -93.84) * mm, "radius": 0.25 * mm});
            skCircle(sketch, "E25.0.1.2", {"center": v(-193.83, -99.44) * mm, "radius": 0.25 * mm});
            skCircle(sketch, "E25.0.1.3", {"center": v(-197.83, -93.84) * mm, "radius": 0.25 * mm});
            skCircle(sketch, "E25.0.2.0", {"center": v(-197.83, -51.04) * mm, "radius": 0.25 * mm});
            skCircle(sketch, "E25.0.2.1", {"center": v(-193.83, -45.44) * mm, "radius": 0.25 * mm});
            skCircle(sketch, "E25.0.2.2", {"center": v(-193.83, -51.04) * mm, "radius": 0.25 * mm});
            skCircle(sketch, "E25.0.2.3", {"center": v(-197.83, -45.44) * mm, "radius": 0.25 * mm});
            skCircle(sketch, "E25.0.3.0", {"center": v(-197.83, -2.64) * mm, "radius": 0.25 * mm});
            skCircle(sketch, "E25.0.3.1", {"center": v(-193.83, 2.96) * mm, "radius": 0.25 * mm});
            skCircle(sketch, "E25.0.3.2", {"center": v(-193.83, -2.64) * mm, "radius": 0.25 * mm});
            skCircle(sketch, "E25.0.3.3", {"center": v(-197.83, 2.96) * mm, "radius": 0.25 * mm});
            skCircle(sketch, "E25.0.4.0", {"center": v(-197.83, 45.76) * mm, "radius": 0.25 * mm});
            skCircle(sketch, "E25.0.4.1", {"center": v(-193.83, 51.36) * mm, "radius": 0.25 * mm});
            skCircle(sketch, "E25.0.4.2", {"center": v(-193.83, 45.76) * mm, "radius": 0.25 * mm});
            skCircle(sketch, "E25.0.4.3", {"center": v(-197.83, 51.36) * mm, "radius": 0.25 * mm});
            skCircle(sketch, "E25.0.5.0", {"center": v(-197.83, 94.16) * mm, "radius": 0.25 * mm});
            skCircle(sketch, "E25.0.5.1", {"center": v(-193.83, 99.76) * mm, "radius": 0.25 * mm});
            skCircle(sketch, "E25.0.5.2", {"center": v(-193.83, 94.16) * mm, "radius": 0.25 * mm});
            skCircle(sketch, "E25.0.5.3", {"center": v(-197.83, 99.76) * mm, "radius": 0.25 * mm});
            skCircle(sketch, "E25.0.6.0", {"center": v(-197.83, 142.56) * mm, "radius": 0.25 * mm});
            skCircle(sketch, "E25.0.6.1", {"center": v(-193.83, 148.16) * mm, "radius": 0.25 * mm});
            skCircle(sketch, "E25.0.6.2", {"center": v(-193.83, 142.56) * mm, "radius": 0.25 * mm});
            skCircle(sketch, "E25.0.6.3", {"center": v(-197.83, 148.16) * mm, "radius": 0.25 * mm});
            skCircle(sketch, "E25.1.0.0", {"center": v(-169.83, -147.84) * mm, "radius": 0.25 * mm});
            skCircle(sketch, "E25.1.0.1", {"center": v(-165.83, -142.24) * mm, "radius": 0.25 * mm});
            skCircle(sketch, "E25.1.0.2", {"center": v(-165.83, -147.84) * mm, "radius": 0.25 * mm});
            skCircle(sketch, "E25.1.0.3", {"center": v(-169.83, -142.24) * mm, "radius": 0.25 * mm});
            skCircle(sketch, "E25.1.1.0", {"center": v(-169.83, -99.44) * mm, "radius": 0.25 * mm});
            skCircle(sketch, "E25.1.1.1", {"center": v(-165.83, -93.84) * mm, "radius": 0.25 * mm});
            skCircle(sketch, "E25.1.1.2", {"center": v(-165.83, -99.44) * mm, "radius": 0.25 * mm});
            skCircle(sketch, "E25.1.1.3", {"center": v(-169.83, -93.84) * mm, "radius": 0.25 * mm});
            skCircle(sketch, "E25.1.2.0", {"center": v(-169.83, -51.04) * mm, "radius": 0.25 * mm});
            skCircle(sketch, "E25.1.2.1", {"center": v(-165.83, -45.44) * mm, "radius": 0.25 * mm});
            skCircle(sketch, "E25.1.2.2", {"center": v(-165.83, -51.04) * mm, "radius": 0.25 * mm});
            skCircle(sketch, "E25.1.2.3", {"center": v(-169.83, -45.44) * mm, "radius": 0.25 * mm});
            skCircle(sketch, "E25.1.3.0", {"center": v(-169.83, -2.64) * mm, "radius": 0.25 * mm});
            skCircle(sketch, "E25.1.3.1", {"center": v(-165.83, 2.96) * mm, "radius": 0.25 * mm});
            skCircle(sketch, "E25.1.3.2", {"center": v(-165.83, -2.64) * mm, "radius": 0.25 * mm});
            skCircle(sketch, "E25.1.3.3", {"center": v(-169.83, 2.96) * mm, "radius": 0.25 * mm});
            skCircle(sketch, "E25.1.4.0", {"center": v(-169.83, 45.76) * mm, "radius": 0.25 * mm});
            skCircle(sketch, "E25.1.4.1", {"center": v(-165.83, 51.36) * mm, "radius": 0.25 * mm});
            skCircle(sketch, "E25.1.4.2", {"center": v(-165.83, 45.76) * mm, "radius": 0.25 * mm});
            skCircle(sketch, "E25.1.4.3", {"center": v(-169.83, 51.36) * mm, "radius": 0.25 * mm});
            skCircle(sketch, "E25.1.5.0", {"center": v(-169.83, 94.16) * mm, "radius": 0.25 * mm});
            skCircle(sketch, "E25.1.5.1", {"center": v(-165.83, 99.76) * mm, "radius": 0.25 * mm});
            skCircle(sketch, "E25.1.5.2", {"center": v(-165.83, 94.16) * mm, "radius": 0.25 * mm});
            skCircle(sketch, "E25.1.5.3", {"center": v(-169.83, 99.76) * mm, "radius": 0.25 * mm});
            skCircle(sketch, "E25.1.6.0", {"center": v(-169.83, 142.56) * mm, "radius": 0.25 * mm});
            skCircle(sketch, "E25.1.6.1", {"center": v(-165.83, 148.16) * mm, "radius": 0.25 * mm});
            skCircle(sketch, "E25.1.6.2", {"center": v(-165.83, 142.56) * mm, "radius": 0.25 * mm});
            skCircle(sketch, "E25.1.6.3", {"center": v(-169.83, 148.16) * mm, "radius": 0.25 * mm});
            skCircle(sketch, "E25.2.0.0", {"center": v(-141.83, -147.84) * mm, "radius": 0.25 * mm});
            skCircle(sketch, "E25.2.0.1", {"center": v(-137.83, -142.24) * mm, "radius": 0.25 * mm});
            skCircle(sketch, "E25.2.0.2", {"center": v(-137.83, -147.84) * mm, "radius": 0.25 * mm});
            skCircle(sketch, "E25.2.0.3", {"center": v(-141.83, -142.24) * mm, "radius": 0.25 * mm});
            skCircle(sketch, "E25.2.1.0", {"center": v(-141.83, -99.44) * mm, "radius": 0.25 * mm});
            skCircle(sketch, "E25.2.1.1", {"center": v(-137.83, -93.84) * mm, "radius": 0.25 * mm});
            skCircle(sketch, "E25.2.1.2", {"center": v(-137.83, -99.44) * mm, "radius": 0.25 * mm});
            skCircle(sketch, "E25.2.1.3", {"center": v(-141.83, -93.84) * mm, "radius": 0.25 * mm});
            skCircle(sketch, "E25.2.2.0", {"center": v(-141.83, -51.04) * mm, "radius": 0.25 * mm});
            skCircle(sketch, "E25.2.2.1", {"center": v(-137.83, -45.44) * mm, "radius": 0.25 * mm});
            skCircle(sketch, "E25.2.2.2", {"center": v(-137.83, -51.04) * mm, "radius": 0.25 * mm});
            skCircle(sketch, "E25.2.2.3", {"center": v(-141.83, -45.44) * mm, "radius": 0.25 * mm});
            skCircle(sketch, "E25.2.3.0", {"center": v(-141.83, -2.64) * mm, "radius": 0.25 * mm});
            skCircle(sketch, "E25.2.3.1", {"center": v(-137.83, 2.96) * mm, "radius": 0.25 * mm});
            skCircle(sketch, "E25.2.3.2", {"center": v(-137.83, -2.64) * mm, "radius": 0.25 * mm});
            skCircle(sketch, "E25.2.3.3", {"center": v(-141.83, 2.96) * mm, "radius": 0.25 * mm});
            skCircle(sketch, "E25.2.4.0", {"center": v(-141.83, 45.76) * mm, "radius": 0.25 * mm});
            skCircle(sketch, "E25.2.4.1", {"center": v(-137.83, 51.36) * mm, "radius": 0.25 * mm});
            skCircle(sketch, "E25.2.4.2", {"center": v(-137.83, 45.76) * mm, "radius": 0.25 * mm});
            skCircle(sketch, "E25.2.4.3", {"center": v(-141.83, 51.36) * mm, "radius": 0.25 * mm});
            skCircle(sketch, "E25.2.5.0", {"center": v(-141.83, 94.16) * mm, "radius": 0.25 * mm});
            skCircle(sketch, "E25.2.5.1", {"center": v(-137.83, 99.76) * mm, "radius": 0.25 * mm});
            skCircle(sketch, "E25.2.5.2", {"center": v(-137.83, 94.16) * mm, "radius": 0.25 * mm});
            skCircle(sketch, "E25.2.5.3", {"center": v(-141.83, 99.76) * mm, "radius": 0.25 * mm});
            skCircle(sketch, "E25.2.6.0", {"center": v(-141.83, 142.56) * mm, "radius": 0.25 * mm});
            skCircle(sketch, "E25.2.6.1", {"center": v(-137.83, 148.16) * mm, "radius": 0.25 * mm});
            skCircle(sketch, "E25.2.6.2", {"center": v(-137.83, 142.56) * mm, "radius": 0.25 * mm});
            skCircle(sketch, "E25.2.6.3", {"center": v(-141.83, 148.16) * mm, "radius": 0.25 * mm});
            skCircle(sketch, "E25.3.0.0", {"center": v(-113.83, -147.84) * mm, "radius": 0.25 * mm});
            skCircle(sketch, "E25.3.0.1", {"center": v(-109.83, -142.24) * mm, "radius": 0.25 * mm});
            skCircle(sketch, "E25.3.0.2", {"center": v(-109.83, -147.84) * mm, "radius": 0.25 * mm});
            skCircle(sketch, "E25.3.0.3", {"center": v(-113.83, -142.24) * mm, "radius": 0.25 * mm});
            skCircle(sketch, "E25.3.1.0", {"center": v(-113.83, -99.44) * mm, "radius": 0.25 * mm});
            skCircle(sketch, "E25.3.1.1", {"center": v(-109.83, -93.84) * mm, "radius": 0.25 * mm});
            skCircle(sketch, "E25.3.1.2", {"center": v(-109.83, -99.44) * mm, "radius": 0.25 * mm});
            skCircle(sketch, "E25.3.1.3", {"center": v(-113.83, -93.84) * mm, "radius": 0.25 * mm});
            skCircle(sketch, "E25.3.2.0", {"center": v(-113.83, -51.04) * mm, "radius": 0.25 * mm});
            skCircle(sketch, "E25.3.2.1", {"center": v(-109.83, -45.44) * mm, "radius": 0.25 * mm});
            skCircle(sketch, "E25.3.2.2", {"center": v(-109.83, -51.04) * mm, "radius": 0.25 * mm});
            skCircle(sketch, "E25.3.2.3", {"center": v(-113.83, -45.44) * mm, "radius": 0.25 * mm});
            skCircle(sketch, "E25.3.3.0", {"center": v(-113.83, -2.64) * mm, "radius": 0.25 * mm});
            skCircle(sketch, "E25.3.3.1", {"center": v(-109.83, 2.96) * mm, "radius": 0.25 * mm});
            skCircle(sketch, "E25.3.3.2", {"center": v(-109.83, -2.64) * mm, "radius": 0.25 * mm});
            skCircle(sketch, "E25.3.3.3", {"center": v(-113.83, 2.96) * mm, "radius": 0.25 * mm});
            skCircle(sketch, "E25.3.4.0", {"center": v(-113.83, 45.76) * mm, "radius": 0.25 * mm});
            skCircle(sketch, "E25.3.4.1", {"center": v(-109.83, 51.36) * mm, "radius": 0.25 * mm});
            skCircle(sketch, "E25.3.4.2", {"center": v(-109.83, 45.76) * mm, "radius": 0.25 * mm});
            skCircle(sketch, "E25.3.4.3", {"center": v(-113.83, 51.36) * mm, "radius": 0.25 * mm});
            skCircle(sketch, "E25.3.5.0", {"center": v(-113.83, 94.16) * mm, "radius": 0.25 * mm});
            skCircle(sketch, "E25.3.5.1", {"center": v(-109.83, 99.76) * mm, "radius": 0.25 * mm});
            skCircle(sketch, "E25.3.5.2", {"center": v(-109.83, 94.16) * mm, "radius": 0.25 * mm});
            skCircle(sketch, "E25.3.5.3", {"center": v(-113.83, 99.76) * mm, "radius": 0.25 * mm});
            skCircle(sketch, "E25.3.6.0", {"center": v(-113.83, 142.56) * mm, "radius": 0.25 * mm});
            skCircle(sketch, "E25.3.6.1", {"center": v(-109.83, 148.16) * mm, "radius": 0.25 * mm});
            skCircle(sketch, "E25.3.6.2", {"center": v(-109.83, 142.56) * mm, "radius": 0.25 * mm});
            skCircle(sketch, "E25.3.6.3", {"center": v(-113.83, 148.16) * mm, "radius": 0.25 * mm});
            skCircle(sketch, "E25.4.0.0", {"center": v(-85.83, -147.84) * mm, "radius": 0.25 * mm});
            skCircle(sketch, "E25.4.0.1", {"center": v(-81.83, -142.24) * mm, "radius": 0.25 * mm});
            skCircle(sketch, "E25.4.0.2", {"center": v(-81.83, -147.84) * mm, "radius": 0.25 * mm});
            skCircle(sketch, "E25.4.0.3", {"center": v(-85.83, -142.24) * mm, "radius": 0.25 * mm});
            skCircle(sketch, "E25.4.1.0", {"center": v(-85.83, -99.44) * mm, "radius": 0.25 * mm});
            skCircle(sketch, "E25.4.1.1", {"center": v(-81.83, -93.84) * mm, "radius": 0.25 * mm});
            skCircle(sketch, "E25.4.1.2", {"center": v(-81.83, -99.44) * mm, "radius": 0.25 * mm});
            skCircle(sketch, "E25.4.1.3", {"center": v(-85.83, -93.84) * mm, "radius": 0.25 * mm});
            skCircle(sketch, "E25.4.2.0", {"center": v(-85.83, -51.04) * mm, "radius": 0.25 * mm});
            skCircle(sketch, "E25.4.2.1", {"center": v(-81.83, -45.44) * mm, "radius": 0.25 * mm});
            skCircle(sketch, "E25.4.2.2", {"center": v(-81.83, -51.04) * mm, "radius": 0.25 * mm});
            skCircle(sketch, "E25.4.2.3", {"center": v(-85.83, -45.44) * mm, "radius": 0.25 * mm});
            skCircle(sketch, "E25.4.3.0", {"center": v(-85.83, -2.64) * mm, "radius": 0.25 * mm});
            skCircle(sketch, "E25.4.3.1", {"center": v(-81.83, 2.96) * mm, "radius": 0.25 * mm});
            skCircle(sketch, "E25.4.3.2", {"center": v(-81.83, -2.64) * mm, "radius": 0.25 * mm});
            skCircle(sketch, "E25.4.3.3", {"center": v(-85.83, 2.96) * mm, "radius": 0.25 * mm});
            skCircle(sketch, "E25.4.4.0", {"center": v(-85.83, 45.76) * mm, "radius": 0.25 * mm});
            skCircle(sketch, "E25.4.4.1", {"center": v(-81.83, 51.36) * mm, "radius": 0.25 * mm});
            skCircle(sketch, "E25.4.4.2", {"center": v(-81.83, 45.76) * mm, "radius": 0.25 * mm});
            skCircle(sketch, "E25.4.4.3", {"center": v(-85.83, 51.36) * mm, "radius": 0.25 * mm});
            skCircle(sketch, "E25.4.5.0", {"center": v(-85.83, 94.16) * mm, "radius": 0.25 * mm});
            skCircle(sketch, "E25.4.5.1", {"center": v(-81.83, 99.76) * mm, "radius": 0.25 * mm});
            skCircle(sketch, "E25.4.5.2", {"center": v(-81.83, 94.16) * mm, "radius": 0.25 * mm});
            skCircle(sketch, "E25.4.5.3", {"center": v(-85.83, 99.76) * mm, "radius": 0.25 * mm});
            skCircle(sketch, "E25.4.6.0", {"center": v(-85.83, 142.56) * mm, "radius": 0.25 * mm});
            skCircle(sketch, "E25.4.6.1", {"center": v(-81.83, 148.16) * mm, "radius": 0.25 * mm});
            skCircle(sketch, "E25.4.6.2", {"center": v(-81.83, 142.56) * mm, "radius": 0.25 * mm});
            skCircle(sketch, "E25.4.6.3", {"center": v(-85.83, 148.16) * mm, "radius": 0.25 * mm});
            skCircle(sketch, "E25.5.0.0", {"center": v(-57.83, -147.84) * mm, "radius": 0.25 * mm});
            skCircle(sketch, "E25.5.0.1", {"center": v(-53.83, -142.24) * mm, "radius": 0.25 * mm});
            skCircle(sketch, "E25.5.0.2", {"center": v(-53.83, -147.84) * mm, "radius": 0.25 * mm});
            skCircle(sketch, "E25.5.0.3", {"center": v(-57.83, -142.24) * mm, "radius": 0.25 * mm});
            skCircle(sketch, "E25.5.1.0", {"center": v(-57.83, -99.44) * mm, "radius": 0.25 * mm});
            skCircle(sketch, "E25.5.1.1", {"center": v(-53.83, -93.84) * mm, "radius": 0.25 * mm});
            skCircle(sketch, "E25.5.1.2", {"center": v(-53.83, -99.44) * mm, "radius": 0.25 * mm});
            skCircle(sketch, "E25.5.1.3", {"center": v(-57.83, -93.84) * mm, "radius": 0.25 * mm});
            skCircle(sketch, "E25.5.2.0", {"center": v(-57.83, -51.04) * mm, "radius": 0.25 * mm});
            skCircle(sketch, "E25.5.2.1", {"center": v(-53.83, -45.44) * mm, "radius": 0.25 * mm});
            skCircle(sketch, "E25.5.2.2", {"center": v(-53.83, -51.04) * mm, "radius": 0.25 * mm});
            skCircle(sketch, "E25.5.2.3", {"center": v(-57.83, -45.44) * mm, "radius": 0.25 * mm});
            skCircle(sketch, "E25.5.3.0", {"center": v(-57.83, -2.64) * mm, "radius": 0.25 * mm});
            skCircle(sketch, "E25.5.3.1", {"center": v(-53.83, 2.96) * mm, "radius": 0.25 * mm});
            skCircle(sketch, "E25.5.3.2", {"center": v(-53.83, -2.64) * mm, "radius": 0.25 * mm});
            skCircle(sketch, "E25.5.3.3", {"center": v(-57.83, 2.96) * mm, "radius": 0.25 * mm});
            skCircle(sketch, "E25.5.4.0", {"center": v(-57.83, 45.76) * mm, "radius": 0.25 * mm});
            skCircle(sketch, "E25.5.4.1", {"center": v(-53.83, 51.36) * mm, "radius": 0.25 * mm});
            skCircle(sketch, "E25.5.4.2", {"center": v(-53.83, 45.76) * mm, "radius": 0.25 * mm});
            skCircle(sketch, "E25.5.4.3", {"center": v(-57.83, 51.36) * mm, "radius": 0.25 * mm});
            skCircle(sketch, "E25.5.5.0", {"center": v(-57.83, 94.16) * mm, "radius": 0.25 * mm});
            skCircle(sketch, "E25.5.5.1", {"center": v(-53.83, 99.76) * mm, "radius": 0.25 * mm});
            skCircle(sketch, "E25.5.5.2", {"center": v(-53.83, 94.16) * mm, "radius": 0.25 * mm});
            skCircle(sketch, "E25.5.5.3", {"center": v(-57.83, 99.76) * mm, "radius": 0.25 * mm});
            skCircle(sketch, "E25.5.6.0", {"center": v(-57.83, 142.56) * mm, "radius": 0.25 * mm});
            skCircle(sketch, "E25.5.6.1", {"center": v(-53.83, 148.16) * mm, "radius": 0.25 * mm});
            skCircle(sketch, "E25.5.6.2", {"center": v(-53.83, 142.56) * mm, "radius": 0.25 * mm});
            skCircle(sketch, "E25.5.6.3", {"center": v(-57.83, 148.16) * mm, "radius": 0.25 * mm});
            skCircle(sketch, "E25.6.0.0", {"center": v(-29.83, -147.84) * mm, "radius": 0.25 * mm});
            skCircle(sketch, "E25.6.0.1", {"center": v(-25.83, -142.24) * mm, "radius": 0.25 * mm});
            skCircle(sketch, "E25.6.0.2", {"center": v(-25.83, -147.84) * mm, "radius": 0.25 * mm});
            skCircle(sketch, "E25.6.0.3", {"center": v(-29.83, -142.24) * mm, "radius": 0.25 * mm});
            skCircle(sketch, "E25.6.1.0", {"center": v(-29.83, -99.44) * mm, "radius": 0.25 * mm});
            skCircle(sketch, "E25.6.1.1", {"center": v(-25.83, -93.84) * mm, "radius": 0.25 * mm});
            skCircle(sketch, "E25.6.1.2", {"center": v(-25.83, -99.44) * mm, "radius": 0.25 * mm});
            skCircle(sketch, "E25.6.1.3", {"center": v(-29.83, -93.84) * mm, "radius": 0.25 * mm});
            skCircle(sketch, "E25.6.2.0", {"center": v(-29.83, -51.04) * mm, "radius": 0.25 * mm});
            skCircle(sketch, "E25.6.2.1", {"center": v(-25.83, -45.44) * mm, "radius": 0.25 * mm});
            skCircle(sketch, "E25.6.2.2", {"center": v(-25.83, -51.04) * mm, "radius": 0.25 * mm});
            skCircle(sketch, "E25.6.2.3", {"center": v(-29.83, -45.44) * mm, "radius": 0.25 * mm});
            skCircle(sketch, "E25.6.3.0", {"center": v(-29.83, -2.64) * mm, "radius": 0.25 * mm});
            skCircle(sketch, "E25.6.3.1", {"center": v(-25.83, 2.96) * mm, "radius": 0.25 * mm});
            skCircle(sketch, "E25.6.3.2", {"center": v(-25.83, -2.64) * mm, "radius": 0.25 * mm});
            skCircle(sketch, "E25.6.3.3", {"center": v(-29.83, 2.96) * mm, "radius": 0.25 * mm});
            skCircle(sketch, "E25.6.4.0", {"center": v(-29.83, 45.76) * mm, "radius": 0.25 * mm});
            skCircle(sketch, "E25.6.4.1", {"center": v(-25.83, 51.36) * mm, "radius": 0.25 * mm});
            skCircle(sketch, "E25.6.4.2", {"center": v(-25.83, 45.76) * mm, "radius": 0.25 * mm});
            skCircle(sketch, "E25.6.4.3", {"center": v(-29.83, 51.36) * mm, "radius": 0.25 * mm});
            skCircle(sketch, "E25.6.5.0", {"center": v(-29.83, 94.16) * mm, "radius": 0.25 * mm});
            skCircle(sketch, "E25.6.5.1", {"center": v(-25.83, 99.76) * mm, "radius": 0.25 * mm});
            skCircle(sketch, "E25.6.5.2", {"center": v(-25.83, 94.16) * mm, "radius": 0.25 * mm});
            skCircle(sketch, "E25.6.5.3", {"center": v(-29.83, 99.76) * mm, "radius": 0.25 * mm});
            skCircle(sketch, "E25.6.6.0", {"center": v(-29.83, 142.56) * mm, "radius": 0.25 * mm});
            skCircle(sketch, "E25.6.6.1", {"center": v(-25.83, 148.16) * mm, "radius": 0.25 * mm});
            skCircle(sketch, "E25.6.6.2", {"center": v(-25.83, 142.56) * mm, "radius": 0.25 * mm});
            skCircle(sketch, "E25.6.6.3", {"center": v(-29.83, 148.16) * mm, "radius": 0.25 * mm});
            skCircle(sketch, "E25.7.0.0", {"center": v(-1.83, -147.84) * mm, "radius": 0.25 * mm});
            skCircle(sketch, "E25.7.0.1", {"center": v(2.17, -142.24) * mm, "radius": 0.25 * mm});
            skCircle(sketch, "E25.7.0.2", {"center": v(2.17, -147.84) * mm, "radius": 0.25 * mm});
            skCircle(sketch, "E25.7.0.3", {"center": v(-1.83, -142.24) * mm, "radius": 0.25 * mm});
            skCircle(sketch, "E25.7.1.0", {"center": v(-1.83, -99.44) * mm, "radius": 0.25 * mm});
            skCircle(sketch, "E25.7.1.1", {"center": v(2.17, -93.84) * mm, "radius": 0.25 * mm});
            skCircle(sketch, "E25.7.1.2", {"center": v(2.17, -99.44) * mm, "radius": 0.25 * mm});
            skCircle(sketch, "E25.7.1.3", {"center": v(-1.83, -93.84) * mm, "radius": 0.25 * mm});
            skCircle(sketch, "E25.7.2.0", {"center": v(-1.83, -51.04) * mm, "radius": 0.25 * mm});
            skCircle(sketch, "E25.7.2.1", {"center": v(2.17, -45.44) * mm, "radius": 0.25 * mm});
            skCircle(sketch, "E25.7.2.2", {"center": v(2.17, -51.04) * mm, "radius": 0.25 * mm});
            skCircle(sketch, "E25.7.2.3", {"center": v(-1.83, -45.44) * mm, "radius": 0.25 * mm});
            skCircle(sketch, "E25.7.3.0", {"center": v(-1.83, -2.64) * mm, "radius": 0.25 * mm});
            skCircle(sketch, "E25.7.3.1", {"center": v(2.17, 2.96) * mm, "radius": 0.25 * mm});
            skCircle(sketch, "E25.7.3.2", {"center": v(2.17, -2.64) * mm, "radius": 0.25 * mm});
            skCircle(sketch, "E25.7.3.3", {"center": v(-1.83, 2.96) * mm, "radius": 0.25 * mm});
            skCircle(sketch, "E25.7.4.0", {"center": v(-1.83, 45.76) * mm, "radius": 0.25 * mm});
            skCircle(sketch, "E25.7.4.1", {"center": v(2.17, 51.36) * mm, "radius": 0.25 * mm});
            skCircle(sketch, "E25.7.4.2", {"center": v(2.17, 45.76) * mm, "radius": 0.25 * mm});
            skCircle(sketch, "E25.7.4.3", {"center": v(-1.83, 51.36) * mm, "radius": 0.25 * mm});
            skCircle(sketch, "E25.7.5.0", {"center": v(-1.83, 94.16) * mm, "radius": 0.25 * mm});
            skCircle(sketch, "E25.7.5.1", {"center": v(2.17, 99.76) * mm, "radius": 0.25 * mm});
            skCircle(sketch, "E25.7.5.2", {"center": v(2.17, 94.16) * mm, "radius": 0.25 * mm});
            skCircle(sketch, "E25.7.5.3", {"center": v(-1.83, 99.76) * mm, "radius": 0.25 * mm});
            skCircle(sketch, "E25.7.6.0", {"center": v(-1.83, 142.56) * mm, "radius": 0.25 * mm});
            skCircle(sketch, "E25.7.6.1", {"center": v(2.17, 148.16) * mm, "radius": 0.25 * mm});
            skCircle(sketch, "E25.7.6.2", {"center": v(2.17, 142.56) * mm, "radius": 0.25 * mm});
            skCircle(sketch, "E25.7.6.3", {"center": v(-1.83, 148.16) * mm, "radius": 0.25 * mm});
            skCircle(sketch, "E25.8.0.0", {"center": v(26.17, -147.84) * mm, "radius": 0.25 * mm});
            skCircle(sketch, "E25.8.0.1", {"center": v(30.17, -142.24) * mm, "radius": 0.25 * mm});
            skCircle(sketch, "E25.8.0.2", {"center": v(30.17, -147.84) * mm, "radius": 0.25 * mm});
            skCircle(sketch, "E25.8.0.3", {"center": v(26.17, -142.24) * mm, "radius": 0.25 * mm});
            skCircle(sketch, "E25.8.1.0", {"center": v(26.17, -99.44) * mm, "radius": 0.25 * mm});
            skCircle(sketch, "E25.8.1.1", {"center": v(30.17, -93.84) * mm, "radius": 0.25 * mm});
            skCircle(sketch, "E25.8.1.2", {"center": v(30.17, -99.44) * mm, "radius": 0.25 * mm});
            skCircle(sketch, "E25.8.1.3", {"center": v(26.17, -93.84) * mm, "radius": 0.25 * mm});
            skCircle(sketch, "E25.8.2.0", {"center": v(26.17, -51.04) * mm, "radius": 0.25 * mm});
            skCircle(sketch, "E25.8.2.1", {"center": v(30.17, -45.44) * mm, "radius": 0.25 * mm});
            skCircle(sketch, "E25.8.2.2", {"center": v(30.17, -51.04) * mm, "radius": 0.25 * mm});
            skCircle(sketch, "E25.8.2.3", {"center": v(26.17, -45.44) * mm, "radius": 0.25 * mm});
            skCircle(sketch, "E25.8.3.0", {"center": v(26.17, -2.64) * mm, "radius": 0.25 * mm});
            skCircle(sketch, "E25.8.3.1", {"center": v(30.17, 2.96) * mm, "radius": 0.25 * mm});
            skCircle(sketch, "E25.8.3.2", {"center": v(30.17, -2.64) * mm, "radius": 0.25 * mm});
            skCircle(sketch, "E25.8.3.3", {"center": v(26.17, 2.96) * mm, "radius": 0.25 * mm});
            skCircle(sketch, "E25.8.4.0", {"center": v(26.17, 45.76) * mm, "radius": 0.25 * mm});
            skCircle(sketch, "E25.8.4.1", {"center": v(30.17, 51.36) * mm, "radius": 0.25 * mm});
            skCircle(sketch, "E25.8.4.2", {"center": v(30.17, 45.76) * mm, "radius": 0.25 * mm});
            skCircle(sketch, "E25.8.4.3", {"center": v(26.17, 51.36) * mm, "radius": 0.25 * mm});
            skCircle(sketch, "E25.8.5.0", {"center": v(26.17, 94.16) * mm, "radius": 0.25 * mm});
            skCircle(sketch, "E25.8.5.1", {"center": v(30.17, 99.76) * mm, "radius": 0.25 * mm});
            skCircle(sketch, "E25.8.5.2", {"center": v(30.17, 94.16) * mm, "radius": 0.25 * mm});
            skCircle(sketch, "E25.8.5.3", {"center": v(26.17, 99.76) * mm, "radius": 0.25 * mm});
            skCircle(sketch, "E25.8.6.0", {"center": v(26.17, 142.56) * mm, "radius": 0.25 * mm});
            skCircle(sketch, "E25.8.6.1", {"center": v(30.17, 148.16) * mm, "radius": 0.25 * mm});
            skCircle(sketch, "E25.8.6.2", {"center": v(30.17, 142.56) * mm, "radius": 0.25 * mm});
            skCircle(sketch, "E25.8.6.3", {"center": v(26.17, 148.16) * mm, "radius": 0.25 * mm});
            skCircle(sketch, "E25.9.0.0", {"center": v(54.17, -147.84) * mm, "radius": 0.25 * mm});
            skCircle(sketch, "E25.9.0.1", {"center": v(58.17, -142.24) * mm, "radius": 0.25 * mm});
            skCircle(sketch, "E25.9.0.2", {"center": v(58.17, -147.84) * mm, "radius": 0.25 * mm});
            skCircle(sketch, "E25.9.0.3", {"center": v(54.17, -142.24) * mm, "radius": 0.25 * mm});
            skCircle(sketch, "E25.9.1.0", {"center": v(54.17, -99.44) * mm, "radius": 0.25 * mm});
            skCircle(sketch, "E25.9.1.1", {"center": v(58.17, -93.84) * mm, "radius": 0.25 * mm});
            skCircle(sketch, "E25.9.1.2", {"center": v(58.17, -99.44) * mm, "radius": 0.25 * mm});
            skCircle(sketch, "E25.9.1.3", {"center": v(54.17, -93.84) * mm, "radius": 0.25 * mm});
            skCircle(sketch, "E25.9.2.0", {"center": v(54.17, -51.04) * mm, "radius": 0.25 * mm});
            skCircle(sketch, "E25.9.2.1", {"center": v(58.17, -45.44) * mm, "radius": 0.25 * mm});
            skCircle(sketch, "E25.9.2.2", {"center": v(58.17, -51.04) * mm, "radius": 0.25 * mm});
            skCircle(sketch, "E25.9.2.3", {"center": v(54.17, -45.44) * mm, "radius": 0.25 * mm});
            skCircle(sketch, "E25.9.3.0", {"center": v(54.17, -2.64) * mm, "radius": 0.25 * mm});
            skCircle(sketch, "E25.9.3.1", {"center": v(58.17, 2.96) * mm, "radius": 0.25 * mm});
            skCircle(sketch, "E25.9.3.2", {"center": v(58.17, -2.64) * mm, "radius": 0.25 * mm});
            skCircle(sketch, "E25.9.3.3", {"center": v(54.17, 2.96) * mm, "radius": 0.25 * mm});
            skCircle(sketch, "E25.9.4.0", {"center": v(54.17, 45.76) * mm, "radius": 0.25 * mm});
            skCircle(sketch, "E25.9.4.1", {"center": v(58.17, 51.36) * mm, "radius": 0.25 * mm});
            skCircle(sketch, "E25.9.4.2", {"center": v(58.17, 45.76) * mm, "radius": 0.25 * mm});
            skCircle(sketch, "E25.9.4.3", {"center": v(54.17, 51.36) * mm, "radius": 0.25 * mm});
            skCircle(sketch, "E25.9.5.0", {"center": v(54.17, 94.16) * mm, "radius": 0.25 * mm});
            skCircle(sketch, "E25.9.5.1", {"center": v(58.17, 99.76) * mm, "radius": 0.25 * mm});
            skCircle(sketch, "E25.9.5.2", {"center": v(58.17, 94.16) * mm, "radius": 0.25 * mm});
            skCircle(sketch, "E25.9.5.3", {"center": v(54.17, 99.76) * mm, "radius": 0.25 * mm});
            skCircle(sketch, "E25.9.6.0", {"center": v(54.17, 142.56) * mm, "radius": 0.25 * mm});
            skCircle(sketch, "E25.9.6.1", {"center": v(58.17, 148.16) * mm, "radius": 0.25 * mm});
            skCircle(sketch, "E25.9.6.2", {"center": v(58.17, 142.56) * mm, "radius": 0.25 * mm});
            skCircle(sketch, "E25.9.6.3", {"center": v(54.17, 148.16) * mm, "radius": 0.25 * mm});
            skCircle(sketch, "E25.10.0.0", {"center": v(82.17, -147.84) * mm, "radius": 0.25 * mm});
            skCircle(sketch, "E25.10.0.1", {"center": v(86.17, -142.24) * mm, "radius": 0.25 * mm});
            skCircle(sketch, "E25.10.0.2", {"center": v(86.17, -147.84) * mm, "radius": 0.25 * mm});
            skCircle(sketch, "E25.10.0.3", {"center": v(82.17, -142.24) * mm, "radius": 0.25 * mm});
            skCircle(sketch, "E25.10.1.0", {"center": v(82.17, -99.44) * mm, "radius": 0.25 * mm});
            skCircle(sketch, "E25.10.1.1", {"center": v(86.17, -93.84) * mm, "radius": 0.25 * mm});
            skCircle(sketch, "E25.10.1.2", {"center": v(86.17, -99.44) * mm, "radius": 0.25 * mm});
            skCircle(sketch, "E25.10.1.3", {"center": v(82.17, -93.84) * mm, "radius": 0.25 * mm});
            skCircle(sketch, "E25.10.2.0", {"center": v(82.17, -51.04) * mm, "radius": 0.25 * mm});
            skCircle(sketch, "E25.10.2.1", {"center": v(86.17, -45.44) * mm, "radius": 0.25 * mm});
            skCircle(sketch, "E25.10.2.2", {"center": v(86.17, -51.04) * mm, "radius": 0.25 * mm});
            skCircle(sketch, "E25.10.2.3", {"center": v(82.17, -45.44) * mm, "radius": 0.25 * mm});
            skCircle(sketch, "E25.10.3.0", {"center": v(82.17, -2.64) * mm, "radius": 0.25 * mm});
            skCircle(sketch, "E25.10.3.1", {"center": v(86.17, 2.96) * mm, "radius": 0.25 * mm});
            skCircle(sketch, "E25.10.3.2", {"center": v(86.17, -2.64) * mm, "radius": 0.25 * mm});
            skCircle(sketch, "E25.10.3.3", {"center": v(82.17, 2.96) * mm, "radius": 0.25 * mm});
            skCircle(sketch, "E25.10.4.0", {"center": v(82.17, 45.76) * mm, "radius": 0.25 * mm});
            skCircle(sketch, "E25.10.4.1", {"center": v(86.17, 51.36) * mm, "radius": 0.25 * mm});
            skCircle(sketch, "E25.10.4.2", {"center": v(86.17, 45.76) * mm, "radius": 0.25 * mm});
            skCircle(sketch, "E25.10.4.3", {"center": v(82.17, 51.36) * mm, "radius": 0.25 * mm});
            skCircle(sketch, "E25.10.5.0", {"center": v(82.17, 94.16) * mm, "radius": 0.25 * mm});
            skCircle(sketch, "E25.10.5.1", {"center": v(86.17, 99.76) * mm, "radius": 0.25 * mm});
            skCircle(sketch, "E25.10.5.2", {"center": v(86.17, 94.16) * mm, "radius": 0.25 * mm});
            skCircle(sketch, "E25.10.5.3", {"center": v(82.17, 99.76) * mm, "radius": 0.25 * mm});
            skCircle(sketch, "E25.10.6.0", {"center": v(82.17, 142.56) * mm, "radius": 0.25 * mm});
            skCircle(sketch, "E25.10.6.1", {"center": v(86.17, 148.16) * mm, "radius": 0.25 * mm});
            skCircle(sketch, "E25.10.6.2", {"center": v(86.17, 142.56) * mm, "radius": 0.25 * mm});
            skCircle(sketch, "E25.10.6.3", {"center": v(82.17, 148.16) * mm, "radius": 0.25 * mm});
            skCircle(sketch, "E25.11.0.0", {"center": v(110.17, -147.84) * mm, "radius": 0.25 * mm});
            skCircle(sketch, "E25.11.0.1", {"center": v(114.17, -142.24) * mm, "radius": 0.25 * mm});
            skCircle(sketch, "E25.11.0.2", {"center": v(114.17, -147.84) * mm, "radius": 0.25 * mm});
            skCircle(sketch, "E25.11.0.3", {"center": v(110.17, -142.24) * mm, "radius": 0.25 * mm});
            skCircle(sketch, "E25.11.1.0", {"center": v(110.17, -99.44) * mm, "radius": 0.25 * mm});
            skCircle(sketch, "E25.11.1.1", {"center": v(114.17, -93.84) * mm, "radius": 0.25 * mm});
            skCircle(sketch, "E25.11.1.2", {"center": v(114.17, -99.44) * mm, "radius": 0.25 * mm});
            skCircle(sketch, "E25.11.1.3", {"center": v(110.17, -93.84) * mm, "radius": 0.25 * mm});
            skCircle(sketch, "E25.11.2.0", {"center": v(110.17, -51.04) * mm, "radius": 0.25 * mm});
            skCircle(sketch, "E25.11.2.1", {"center": v(114.17, -45.44) * mm, "radius": 0.25 * mm});
            skCircle(sketch, "E25.11.2.2", {"center": v(114.17, -51.04) * mm, "radius": 0.25 * mm});
            skCircle(sketch, "E25.11.2.3", {"center": v(110.17, -45.44) * mm, "radius": 0.25 * mm});
            skCircle(sketch, "E25.11.3.0", {"center": v(110.17, -2.64) * mm, "radius": 0.25 * mm});
            skCircle(sketch, "E25.11.3.1", {"center": v(114.17, 2.96) * mm, "radius": 0.25 * mm});
            skCircle(sketch, "E25.11.3.2", {"center": v(114.17, -2.64) * mm, "radius": 0.25 * mm});
            skCircle(sketch, "E25.11.3.3", {"center": v(110.17, 2.96) * mm, "radius": 0.25 * mm});
            skCircle(sketch, "E25.11.4.0", {"center": v(110.17, 45.76) * mm, "radius": 0.25 * mm});
            skCircle(sketch, "E25.11.4.1", {"center": v(114.17, 51.36) * mm, "radius": 0.25 * mm});
            skCircle(sketch, "E25.11.4.2", {"center": v(114.17, 45.76) * mm, "radius": 0.25 * mm});
            skCircle(sketch, "E25.11.4.3", {"center": v(110.17, 51.36) * mm, "radius": 0.25 * mm});
            skCircle(sketch, "E25.11.5.0", {"center": v(110.17, 94.16) * mm, "radius": 0.25 * mm});
            skCircle(sketch, "E25.11.5.1", {"center": v(114.17, 99.76) * mm, "radius": 0.25 * mm});
            skCircle(sketch, "E25.11.5.2", {"center": v(114.17, 94.16) * mm, "radius": 0.25 * mm});
            skCircle(sketch, "E25.11.5.3", {"center": v(110.17, 99.76) * mm, "radius": 0.25 * mm});
            skCircle(sketch, "E25.11.6.0", {"center": v(110.17, 142.56) * mm, "radius": 0.25 * mm});
            skCircle(sketch, "E25.11.6.1", {"center": v(114.17, 148.16) * mm, "radius": 0.25 * mm});
            skCircle(sketch, "E25.11.6.2", {"center": v(114.17, 142.56) * mm, "radius": 0.25 * mm});
            skCircle(sketch, "E25.11.6.3", {"center": v(110.17, 148.16) * mm, "radius": 0.25 * mm});
            skCircle(sketch, "E25.12.0.0", {"center": v(138.17, -147.84) * mm, "radius": 0.25 * mm});
            skCircle(sketch, "E25.12.0.1", {"center": v(142.17, -142.24) * mm, "radius": 0.25 * mm});
            skCircle(sketch, "E25.12.0.2", {"center": v(142.17, -147.84) * mm, "radius": 0.25 * mm});
            skCircle(sketch, "E25.12.0.3", {"center": v(138.17, -142.24) * mm, "radius": 0.25 * mm});
            skCircle(sketch, "E25.12.1.0", {"center": v(138.17, -99.44) * mm, "radius": 0.25 * mm});
            skCircle(sketch, "E25.12.1.1", {"center": v(142.17, -93.84) * mm, "radius": 0.25 * mm});
            skCircle(sketch, "E25.12.1.2", {"center": v(142.17, -99.44) * mm, "radius": 0.25 * mm});
            skCircle(sketch, "E25.12.1.3", {"center": v(138.17, -93.84) * mm, "radius": 0.25 * mm});
            skCircle(sketch, "E25.12.2.0", {"center": v(138.17, -51.04) * mm, "radius": 0.25 * mm});
            skCircle(sketch, "E25.12.2.1", {"center": v(142.17, -45.44) * mm, "radius": 0.25 * mm});
            skCircle(sketch, "E25.12.2.2", {"center": v(142.17, -51.04) * mm, "radius": 0.25 * mm});
            skCircle(sketch, "E25.12.2.3", {"center": v(138.17, -45.44) * mm, "radius": 0.25 * mm});
            skCircle(sketch, "E25.12.3.0", {"center": v(138.17, -2.64) * mm, "radius": 0.25 * mm});
            skCircle(sketch, "E25.12.3.1", {"center": v(142.17, 2.96) * mm, "radius": 0.25 * mm});
            skCircle(sketch, "E25.12.3.2", {"center": v(142.17, -2.64) * mm, "radius": 0.25 * mm});
            skCircle(sketch, "E25.12.3.3", {"center": v(138.17, 2.96) * mm, "radius": 0.25 * mm});
            skCircle(sketch, "E25.12.4.0", {"center": v(138.17, 45.76) * mm, "radius": 0.25 * mm});
            skCircle(sketch, "E25.12.4.1", {"center": v(142.17, 51.36) * mm, "radius": 0.25 * mm});
            skCircle(sketch, "E25.12.4.2", {"center": v(142.17, 45.76) * mm, "radius": 0.25 * mm});
            skCircle(sketch, "E25.12.4.3", {"center": v(138.17, 51.36) * mm, "radius": 0.25 * mm});
            skCircle(sketch, "E25.12.5.0", {"center": v(138.17, 94.16) * mm, "radius": 0.25 * mm});
            skCircle(sketch, "E25.12.5.1", {"center": v(142.17, 99.76) * mm, "radius": 0.25 * mm});
            skCircle(sketch, "E25.12.5.2", {"center": v(142.17, 94.16) * mm, "radius": 0.25 * mm});
            skCircle(sketch, "E25.12.5.3", {"center": v(138.17, 99.76) * mm, "radius": 0.25 * mm});
            skCircle(sketch, "E25.12.6.0", {"center": v(138.17, 142.56) * mm, "radius": 0.25 * mm});
            skCircle(sketch, "E25.12.6.1", {"center": v(142.17, 148.16) * mm, "radius": 0.25 * mm});
            skCircle(sketch, "E25.12.6.2", {"center": v(142.17, 142.56) * mm, "radius": 0.25 * mm});
            skCircle(sketch, "E25.12.6.3", {"center": v(138.17, 148.16) * mm, "radius": 0.25 * mm});
            skCircle(sketch, "E25.13.0.0", {"center": v(166.17, -147.84) * mm, "radius": 0.25 * mm});
            skCircle(sketch, "E25.13.0.1", {"center": v(170.17, -142.24) * mm, "radius": 0.25 * mm});
            skCircle(sketch, "E25.13.0.2", {"center": v(170.17, -147.84) * mm, "radius": 0.25 * mm});
            skCircle(sketch, "E25.13.0.3", {"center": v(166.17, -142.24) * mm, "radius": 0.25 * mm});
            skCircle(sketch, "E25.13.1.0", {"center": v(166.17, -99.44) * mm, "radius": 0.25 * mm});
            skCircle(sketch, "E25.13.1.1", {"center": v(170.17, -93.84) * mm, "radius": 0.25 * mm});
            skCircle(sketch, "E25.13.1.2", {"center": v(170.17, -99.44) * mm, "radius": 0.25 * mm});
            skCircle(sketch, "E25.13.1.3", {"center": v(166.17, -93.84) * mm, "radius": 0.25 * mm});
            skCircle(sketch, "E25.13.2.0", {"center": v(166.17, -51.04) * mm, "radius": 0.25 * mm});
            skCircle(sketch, "E25.13.2.1", {"center": v(170.17, -45.44) * mm, "radius": 0.25 * mm});
            skCircle(sketch, "E25.13.2.2", {"center": v(170.17, -51.04) * mm, "radius": 0.25 * mm});
            skCircle(sketch, "E25.13.2.3", {"center": v(166.17, -45.44) * mm, "radius": 0.25 * mm});
            skCircle(sketch, "E25.13.3.0", {"center": v(166.17, -2.64) * mm, "radius": 0.25 * mm});
            skCircle(sketch, "E25.13.3.1", {"center": v(170.17, 2.96) * mm, "radius": 0.25 * mm});
            skCircle(sketch, "E25.13.3.2", {"center": v(170.17, -2.64) * mm, "radius": 0.25 * mm});
            skCircle(sketch, "E25.13.3.3", {"center": v(166.17, 2.96) * mm, "radius": 0.25 * mm});
            skCircle(sketch, "E25.13.4.0", {"center": v(166.17, 45.76) * mm, "radius": 0.25 * mm});
            skCircle(sketch, "E25.13.4.1", {"center": v(170.17, 51.36) * mm, "radius": 0.25 * mm});
            skCircle(sketch, "E25.13.4.2", {"center": v(170.17, 45.76) * mm, "radius": 0.25 * mm});
            skCircle(sketch, "E25.13.4.3", {"center": v(166.17, 51.36) * mm, "radius": 0.25 * mm});
            skCircle(sketch, "E25.13.5.0", {"center": v(166.17, 94.16) * mm, "radius": 0.25 * mm});
            skCircle(sketch, "E25.13.5.1", {"center": v(170.17, 99.76) * mm, "radius": 0.25 * mm});
            skCircle(sketch, "E25.13.5.2", {"center": v(170.17, 94.16) * mm, "radius": 0.25 * mm});
            skCircle(sketch, "E25.13.5.3", {"center": v(166.17, 99.76) * mm, "radius": 0.25 * mm});
            skCircle(sketch, "E25.13.6.0", {"center": v(166.17, 142.56) * mm, "radius": 0.25 * mm});
            skCircle(sketch, "E25.13.6.1", {"center": v(170.17, 148.16) * mm, "radius": 0.25 * mm});
            skCircle(sketch, "E25.13.6.2", {"center": v(170.17, 142.56) * mm, "radius": 0.25 * mm});
            skCircle(sketch, "E25.13.6.3", {"center": v(166.17, 148.16) * mm, "radius": 0.25 * mm});
            skCircle(sketch, "E25.14.0.0", {"center": v(194.17, -147.84) * mm, "radius": 0.25 * mm});
            skCircle(sketch, "E25.14.0.1", {"center": v(198.17, -142.24) * mm, "radius": 0.25 * mm});
            skCircle(sketch, "E25.14.0.2", {"center": v(198.17, -147.84) * mm, "radius": 0.25 * mm});
            skCircle(sketch, "E25.14.0.3", {"center": v(194.17, -142.24) * mm, "radius": 0.25 * mm});
            skCircle(sketch, "E25.14.1.0", {"center": v(194.17, -99.44) * mm, "radius": 0.25 * mm});
            skCircle(sketch, "E25.14.1.1", {"center": v(198.17, -93.84) * mm, "radius": 0.25 * mm});
            skCircle(sketch, "E25.14.1.2", {"center": v(198.17, -99.44) * mm, "radius": 0.25 * mm});
            skCircle(sketch, "E25.14.1.3", {"center": v(194.17, -93.84) * mm, "radius": 0.25 * mm});
            skCircle(sketch, "E25.14.2.0", {"center": v(194.17, -51.04) * mm, "radius": 0.25 * mm});
            skCircle(sketch, "E25.14.2.1", {"center": v(198.17, -45.44) * mm, "radius": 0.25 * mm});
            skCircle(sketch, "E25.14.2.2", {"center": v(198.17, -51.04) * mm, "radius": 0.25 * mm});
            skCircle(sketch, "E25.14.2.3", {"center": v(194.17, -45.44) * mm, "radius": 0.25 * mm});
            skCircle(sketch, "E25.14.3.0", {"center": v(194.17, -2.64) * mm, "radius": 0.25 * mm});
            skCircle(sketch, "E25.14.3.1", {"center": v(198.17, 2.96) * mm, "radius": 0.25 * mm});
            skCircle(sketch, "E25.14.3.2", {"center": v(198.17, -2.64) * mm, "radius": 0.25 * mm});
            skCircle(sketch, "E25.14.3.3", {"center": v(194.17, 2.96) * mm, "radius": 0.25 * mm});
            skCircle(sketch, "E25.14.4.0", {"center": v(194.17, 45.76) * mm, "radius": 0.25 * mm});
            skCircle(sketch, "E25.14.4.1", {"center": v(198.17, 51.36) * mm, "radius": 0.25 * mm});
            skCircle(sketch, "E25.14.4.2", {"center": v(198.17, 45.76) * mm, "radius": 0.25 * mm});
            skCircle(sketch, "E25.14.4.3", {"center": v(194.17, 51.36) * mm, "radius": 0.25 * mm});
            skCircle(sketch, "E25.14.5.0", {"center": v(194.17, 94.16) * mm, "radius": 0.25 * mm});
            skCircle(sketch, "E25.14.5.1", {"center": v(198.17, 99.76) * mm, "radius": 0.25 * mm});
            skCircle(sketch, "E25.14.5.2", {"center": v(198.17, 94.16) * mm, "radius": 0.25 * mm});
            skCircle(sketch, "E25.14.5.3", {"center": v(194.17, 99.76) * mm, "radius": 0.25 * mm});
            skCircle(sketch, "E25.14.6.0", {"center": v(194.17, 142.56) * mm, "radius": 0.25 * mm});
            skCircle(sketch, "E25.14.6.1", {"center": v(198.17, 148.16) * mm, "radius": 0.25 * mm});
            skCircle(sketch, "E25.14.6.2", {"center": v(198.17, 142.56) * mm, "radius": 0.25 * mm});
            skCircle(sketch, "E25.14.6.3", {"center": v(194.17, 148.16) * mm, "radius": 0.25 * mm});
            skLineSegment(sketch, "E25.direction1", {"start": v(-197.83, -147.84) * mm, "end": v(-169.83, -147.84) * mm, "construction": true});
            skLineSegment(sketch, "E25.direction2", {"start": v(-197.83, -147.84) * mm, "end": v(-197.83, -99.44) * mm, "construction": true});
            skCircle(sketch, "E26.0.1.0", {"center": v(-183.85, -69.5) * mm, "radius": 0.25 * mm});
            skCircle(sketch, "E26.0.1.1", {"center": v(-179.85, -69.5) * mm, "radius": 0.25 * mm});
            skCircle(sketch, "E26.0.1.2", {"center": v(-183.85, -75.1) * mm, "radius": 0.25 * mm});
            skCircle(sketch, "E26.0.1.3", {"center": v(-179.85, -75.1) * mm, "radius": 0.25 * mm});
            skCircle(sketch, "E26.0.2.0", {"center": v(-183.85, -21.1) * mm, "radius": 0.25 * mm});
            skCircle(sketch, "E26.0.2.1", {"center": v(-179.85, -21.1) * mm, "radius": 0.25 * mm});
            skCircle(sketch, "E26.0.2.2", {"center": v(-183.85, -26.7) * mm, "radius": 0.25 * mm});
            skCircle(sketch, "E26.0.2.3", {"center": v(-179.85, -26.7) * mm, "radius": 0.25 * mm});
            skCircle(sketch, "E26.0.3.0", {"center": v(-183.85, 27.3) * mm, "radius": 0.25 * mm});
            skCircle(sketch, "E26.0.3.1", {"center": v(-179.85, 27.3) * mm, "radius": 0.25 * mm});
            skCircle(sketch, "E26.0.3.2", {"center": v(-183.85, 21.7) * mm, "radius": 0.25 * mm});
            skCircle(sketch, "E26.0.3.3", {"center": v(-179.85, 21.7) * mm, "radius": 0.25 * mm});
            skCircle(sketch, "E26.0.4.0", {"center": v(-183.85, 75.7) * mm, "radius": 0.25 * mm});
            skCircle(sketch, "E26.0.4.1", {"center": v(-179.85, 75.7) * mm, "radius": 0.25 * mm});
            skCircle(sketch, "E26.0.4.2", {"center": v(-183.85, 70.1) * mm, "radius": 0.25 * mm});
            skCircle(sketch, "E26.0.4.3", {"center": v(-179.85, 70.1) * mm, "radius": 0.25 * mm});
            skCircle(sketch, "E26.0.5.0", {"center": v(-183.85, 124.1) * mm, "radius": 0.25 * mm});
            skCircle(sketch, "E26.0.5.1", {"center": v(-179.85, 124.1) * mm, "radius": 0.25 * mm});
            skCircle(sketch, "E26.0.5.2", {"center": v(-183.85, 118.5) * mm, "radius": 0.25 * mm});
            skCircle(sketch, "E26.0.5.3", {"center": v(-179.85, 118.5) * mm, "radius": 0.25 * mm});
            skCircle(sketch, "E26.1.0.0", {"center": v(-155.85, -117.9) * mm, "radius": 0.25 * mm});
            skCircle(sketch, "E26.1.0.1", {"center": v(-151.85, -117.9) * mm, "radius": 0.25 * mm});
            skCircle(sketch, "E26.1.0.2", {"center": v(-155.85, -123.5) * mm, "radius": 0.25 * mm});
            skCircle(sketch, "E26.1.0.3", {"center": v(-151.85, -123.5) * mm, "radius": 0.25 * mm});
            skCircle(sketch, "E26.1.1.0", {"center": v(-155.85, -69.5) * mm, "radius": 0.25 * mm});
            skCircle(sketch, "E26.1.1.1", {"center": v(-151.85, -69.5) * mm, "radius": 0.25 * mm});
            skCircle(sketch, "E26.1.1.2", {"center": v(-155.85, -75.1) * mm, "radius": 0.25 * mm});
            skCircle(sketch, "E26.1.1.3", {"center": v(-151.85, -75.1) * mm, "radius": 0.25 * mm});
            skCircle(sketch, "E26.1.2.0", {"center": v(-155.85, -21.1) * mm, "radius": 0.25 * mm});
            skCircle(sketch, "E26.1.2.1", {"center": v(-151.85, -21.1) * mm, "radius": 0.25 * mm});
            skCircle(sketch, "E26.1.2.2", {"center": v(-155.85, -26.7) * mm, "radius": 0.25 * mm});
            skCircle(sketch, "E26.1.2.3", {"center": v(-151.85, -26.7) * mm, "radius": 0.25 * mm});
            skCircle(sketch, "E26.1.3.0", {"center": v(-155.85, 27.3) * mm, "radius": 0.25 * mm});
            skCircle(sketch, "E26.1.3.1", {"center": v(-151.85, 27.3) * mm, "radius": 0.25 * mm});
            skCircle(sketch, "E26.1.3.2", {"center": v(-155.85, 21.7) * mm, "radius": 0.25 * mm});
            skCircle(sketch, "E26.1.3.3", {"center": v(-151.85, 21.7) * mm, "radius": 0.25 * mm});
            skCircle(sketch, "E26.1.4.0", {"center": v(-155.85, 75.7) * mm, "radius": 0.25 * mm});
            skCircle(sketch, "E26.1.4.1", {"center": v(-151.85, 75.7) * mm, "radius": 0.25 * mm});
            skCircle(sketch, "E26.1.4.2", {"center": v(-155.85, 70.1) * mm, "radius": 0.25 * mm});
            skCircle(sketch, "E26.1.4.3", {"center": v(-151.85, 70.1) * mm, "radius": 0.25 * mm});
            skCircle(sketch, "E26.1.5.0", {"center": v(-155.85, 124.1) * mm, "radius": 0.25 * mm});
            skCircle(sketch, "E26.1.5.1", {"center": v(-151.85, 124.1) * mm, "radius": 0.25 * mm});
            skCircle(sketch, "E26.1.5.2", {"center": v(-155.85, 118.5) * mm, "radius": 0.25 * mm});
            skCircle(sketch, "E26.1.5.3", {"center": v(-151.85, 118.5) * mm, "radius": 0.25 * mm});
            skCircle(sketch, "E26.2.0.0", {"center": v(-127.85, -117.9) * mm, "radius": 0.25 * mm});
            skCircle(sketch, "E26.2.0.1", {"center": v(-123.85, -117.9) * mm, "radius": 0.25 * mm});
            skCircle(sketch, "E26.2.0.2", {"center": v(-127.85, -123.5) * mm, "radius": 0.25 * mm});
            skCircle(sketch, "E26.2.0.3", {"center": v(-123.85, -123.5) * mm, "radius": 0.25 * mm});
            skCircle(sketch, "E26.2.1.0", {"center": v(-127.85, -69.5) * mm, "radius": 0.25 * mm});
            skCircle(sketch, "E26.2.1.1", {"center": v(-123.85, -69.5) * mm, "radius": 0.25 * mm});
            skCircle(sketch, "E26.2.1.2", {"center": v(-127.85, -75.1) * mm, "radius": 0.25 * mm});
            skCircle(sketch, "E26.2.1.3", {"center": v(-123.85, -75.1) * mm, "radius": 0.25 * mm});
            skCircle(sketch, "E26.2.2.0", {"center": v(-127.85, -21.1) * mm, "radius": 0.25 * mm});
            skCircle(sketch, "E26.2.2.1", {"center": v(-123.85, -21.1) * mm, "radius": 0.25 * mm});
            skCircle(sketch, "E26.2.2.2", {"center": v(-127.85, -26.7) * mm, "radius": 0.25 * mm});
            skCircle(sketch, "E26.2.2.3", {"center": v(-123.85, -26.7) * mm, "radius": 0.25 * mm});
            skCircle(sketch, "E26.2.3.0", {"center": v(-127.85, 27.3) * mm, "radius": 0.25 * mm});
            skCircle(sketch, "E26.2.3.1", {"center": v(-123.85, 27.3) * mm, "radius": 0.25 * mm});
            skCircle(sketch, "E26.2.3.2", {"center": v(-127.85, 21.7) * mm, "radius": 0.25 * mm});
            skCircle(sketch, "E26.2.3.3", {"center": v(-123.85, 21.7) * mm, "radius": 0.25 * mm});
            skCircle(sketch, "E26.2.4.0", {"center": v(-127.85, 75.7) * mm, "radius": 0.25 * mm});
            skCircle(sketch, "E26.2.4.1", {"center": v(-123.85, 75.7) * mm, "radius": 0.25 * mm});
            skCircle(sketch, "E26.2.4.2", {"center": v(-127.85, 70.1) * mm, "radius": 0.25 * mm});
            skCircle(sketch, "E26.2.4.3", {"center": v(-123.85, 70.1) * mm, "radius": 0.25 * mm});
            skCircle(sketch, "E26.2.5.0", {"center": v(-127.85, 124.1) * mm, "radius": 0.25 * mm});
            skCircle(sketch, "E26.2.5.1", {"center": v(-123.85, 124.1) * mm, "radius": 0.25 * mm});
            skCircle(sketch, "E26.2.5.2", {"center": v(-127.85, 118.5) * mm, "radius": 0.25 * mm});
            skCircle(sketch, "E26.2.5.3", {"center": v(-123.85, 118.5) * mm, "radius": 0.25 * mm});
            skCircle(sketch, "E26.3.0.0", {"center": v(-99.85, -117.9) * mm, "radius": 0.25 * mm});
            skCircle(sketch, "E26.3.0.1", {"center": v(-95.85, -117.9) * mm, "radius": 0.25 * mm});
            skCircle(sketch, "E26.3.0.2", {"center": v(-99.85, -123.5) * mm, "radius": 0.25 * mm});
            skCircle(sketch, "E26.3.0.3", {"center": v(-95.85, -123.5) * mm, "radius": 0.25 * mm});
            skCircle(sketch, "E26.3.1.0", {"center": v(-99.85, -69.5) * mm, "radius": 0.25 * mm});
            skCircle(sketch, "E26.3.1.1", {"center": v(-95.85, -69.5) * mm, "radius": 0.25 * mm});
            skCircle(sketch, "E26.3.1.2", {"center": v(-99.85, -75.1) * mm, "radius": 0.25 * mm});
            skCircle(sketch, "E26.3.1.3", {"center": v(-95.85, -75.1) * mm, "radius": 0.25 * mm});
            skCircle(sketch, "E26.3.2.0", {"center": v(-99.85, -21.1) * mm, "radius": 0.25 * mm});
            skCircle(sketch, "E26.3.2.1", {"center": v(-95.85, -21.1) * mm, "radius": 0.25 * mm});
            skCircle(sketch, "E26.3.2.2", {"center": v(-99.85, -26.7) * mm, "radius": 0.25 * mm});
            skCircle(sketch, "E26.3.2.3", {"center": v(-95.85, -26.7) * mm, "radius": 0.25 * mm});
            skCircle(sketch, "E26.3.3.0", {"center": v(-99.85, 27.3) * mm, "radius": 0.25 * mm});
            skCircle(sketch, "E26.3.3.1", {"center": v(-95.85, 27.3) * mm, "radius": 0.25 * mm});
            skCircle(sketch, "E26.3.3.2", {"center": v(-99.85, 21.7) * mm, "radius": 0.25 * mm});
            skCircle(sketch, "E26.3.3.3", {"center": v(-95.85, 21.7) * mm, "radius": 0.25 * mm});
            skCircle(sketch, "E26.3.4.0", {"center": v(-99.85, 75.7) * mm, "radius": 0.25 * mm});
            skCircle(sketch, "E26.3.4.1", {"center": v(-95.85, 75.7) * mm, "radius": 0.25 * mm});
            skCircle(sketch, "E26.3.4.2", {"center": v(-99.85, 70.1) * mm, "radius": 0.25 * mm});
            skCircle(sketch, "E26.3.4.3", {"center": v(-95.85, 70.1) * mm, "radius": 0.25 * mm});
            skCircle(sketch, "E26.3.5.0", {"center": v(-99.85, 124.1) * mm, "radius": 0.25 * mm});
            skCircle(sketch, "E26.3.5.1", {"center": v(-95.85, 124.1) * mm, "radius": 0.25 * mm});
            skCircle(sketch, "E26.3.5.2", {"center": v(-99.85, 118.5) * mm, "radius": 0.25 * mm});
            skCircle(sketch, "E26.3.5.3", {"center": v(-95.85, 118.5) * mm, "radius": 0.25 * mm});
            skCircle(sketch, "E26.4.0.0", {"center": v(-71.85, -117.9) * mm, "radius": 0.25 * mm});
            skCircle(sketch, "E26.4.0.1", {"center": v(-67.85, -117.9) * mm, "radius": 0.25 * mm});
            skCircle(sketch, "E26.4.0.2", {"center": v(-71.85, -123.5) * mm, "radius": 0.25 * mm});
            skCircle(sketch, "E26.4.0.3", {"center": v(-67.85, -123.5) * mm, "radius": 0.25 * mm});
            skCircle(sketch, "E26.4.1.0", {"center": v(-71.85, -69.5) * mm, "radius": 0.25 * mm});
            skCircle(sketch, "E26.4.1.1", {"center": v(-67.85, -69.5) * mm, "radius": 0.25 * mm});
            skCircle(sketch, "E26.4.1.2", {"center": v(-71.85, -75.1) * mm, "radius": 0.25 * mm});
            skCircle(sketch, "E26.4.1.3", {"center": v(-67.85, -75.1) * mm, "radius": 0.25 * mm});
            skCircle(sketch, "E26.4.2.0", {"center": v(-71.85, -21.1) * mm, "radius": 0.25 * mm});
            skCircle(sketch, "E26.4.2.1", {"center": v(-67.85, -21.1) * mm, "radius": 0.25 * mm});
            skCircle(sketch, "E26.4.2.2", {"center": v(-71.85, -26.7) * mm, "radius": 0.25 * mm});
            skCircle(sketch, "E26.4.2.3", {"center": v(-67.85, -26.7) * mm, "radius": 0.25 * mm});
            skCircle(sketch, "E26.4.3.0", {"center": v(-71.85, 27.3) * mm, "radius": 0.25 * mm});
            skCircle(sketch, "E26.4.3.1", {"center": v(-67.85, 27.3) * mm, "radius": 0.25 * mm});
            skCircle(sketch, "E26.4.3.2", {"center": v(-71.85, 21.7) * mm, "radius": 0.25 * mm});
            skCircle(sketch, "E26.4.3.3", {"center": v(-67.85, 21.7) * mm, "radius": 0.25 * mm});
            skCircle(sketch, "E26.4.4.0", {"center": v(-71.85, 75.7) * mm, "radius": 0.25 * mm});
            skCircle(sketch, "E26.4.4.1", {"center": v(-67.85, 75.7) * mm, "radius": 0.25 * mm});
            skCircle(sketch, "E26.4.4.2", {"center": v(-71.85, 70.1) * mm, "radius": 0.25 * mm});
            skCircle(sketch, "E26.4.4.3", {"center": v(-67.85, 70.1) * mm, "radius": 0.25 * mm});
            skCircle(sketch, "E26.4.5.0", {"center": v(-71.85, 124.1) * mm, "radius": 0.25 * mm});
            skCircle(sketch, "E26.4.5.1", {"center": v(-67.85, 124.1) * mm, "radius": 0.25 * mm});
            skCircle(sketch, "E26.4.5.2", {"center": v(-71.85, 118.5) * mm, "radius": 0.25 * mm});
            skCircle(sketch, "E26.4.5.3", {"center": v(-67.85, 118.5) * mm, "radius": 0.25 * mm});
            skCircle(sketch, "E26.5.0.0", {"center": v(-43.85, -117.9) * mm, "radius": 0.25 * mm});
            skCircle(sketch, "E26.5.0.1", {"center": v(-39.85, -117.9) * mm, "radius": 0.25 * mm});
            skCircle(sketch, "E26.5.0.2", {"center": v(-43.85, -123.5) * mm, "radius": 0.25 * mm});
            skCircle(sketch, "E26.5.0.3", {"center": v(-39.85, -123.5) * mm, "radius": 0.25 * mm});
            skCircle(sketch, "E26.5.1.0", {"center": v(-43.85, -69.5) * mm, "radius": 0.25 * mm});
            skCircle(sketch, "E26.5.1.1", {"center": v(-39.85, -69.5) * mm, "radius": 0.25 * mm});
            skCircle(sketch, "E26.5.1.2", {"center": v(-43.85, -75.1) * mm, "radius": 0.25 * mm});
            skCircle(sketch, "E26.5.1.3", {"center": v(-39.85, -75.1) * mm, "radius": 0.25 * mm});
            skCircle(sketch, "E26.5.2.0", {"center": v(-43.85, -21.1) * mm, "radius": 0.25 * mm});
            skCircle(sketch, "E26.5.2.1", {"center": v(-39.85, -21.1) * mm, "radius": 0.25 * mm});
            skCircle(sketch, "E26.5.2.2", {"center": v(-43.85, -26.7) * mm, "radius": 0.25 * mm});
            skCircle(sketch, "E26.5.2.3", {"center": v(-39.85, -26.7) * mm, "radius": 0.25 * mm});
            skCircle(sketch, "E26.5.3.0", {"center": v(-43.85, 27.3) * mm, "radius": 0.25 * mm});
            skCircle(sketch, "E26.5.3.1", {"center": v(-39.85, 27.3) * mm, "radius": 0.25 * mm});
            skCircle(sketch, "E26.5.3.2", {"center": v(-43.85, 21.7) * mm, "radius": 0.25 * mm});
            skCircle(sketch, "E26.5.3.3", {"center": v(-39.85, 21.7) * mm, "radius": 0.25 * mm});
            skCircle(sketch, "E26.5.4.0", {"center": v(-43.85, 75.7) * mm, "radius": 0.25 * mm});
            skCircle(sketch, "E26.5.4.1", {"center": v(-39.85, 75.7) * mm, "radius": 0.25 * mm});
            skCircle(sketch, "E26.5.4.2", {"center": v(-43.85, 70.1) * mm, "radius": 0.25 * mm});
            skCircle(sketch, "E26.5.4.3", {"center": v(-39.85, 70.1) * mm, "radius": 0.25 * mm});
            skCircle(sketch, "E26.5.5.0", {"center": v(-43.85, 124.1) * mm, "radius": 0.25 * mm});
            skCircle(sketch, "E26.5.5.1", {"center": v(-39.85, 124.1) * mm, "radius": 0.25 * mm});
            skCircle(sketch, "E26.5.5.2", {"center": v(-43.85, 118.5) * mm, "radius": 0.25 * mm});
            skCircle(sketch, "E26.5.5.3", {"center": v(-39.85, 118.5) * mm, "radius": 0.25 * mm});
            skCircle(sketch, "E26.6.0.0", {"center": v(-15.85, -117.9) * mm, "radius": 0.25 * mm});
            skCircle(sketch, "E26.6.0.1", {"center": v(-11.85, -117.9) * mm, "radius": 0.25 * mm});
            skCircle(sketch, "E26.6.0.2", {"center": v(-15.85, -123.5) * mm, "radius": 0.25 * mm});
            skCircle(sketch, "E26.6.0.3", {"center": v(-11.85, -123.5) * mm, "radius": 0.25 * mm});
            skCircle(sketch, "E26.6.1.0", {"center": v(-15.85, -69.5) * mm, "radius": 0.25 * mm});
            skCircle(sketch, "E26.6.1.1", {"center": v(-11.85, -69.5) * mm, "radius": 0.25 * mm});
            skCircle(sketch, "E26.6.1.2", {"center": v(-15.85, -75.1) * mm, "radius": 0.25 * mm});
            skCircle(sketch, "E26.6.1.3", {"center": v(-11.85, -75.1) * mm, "radius": 0.25 * mm});
            skCircle(sketch, "E26.6.2.0", {"center": v(-15.85, -21.1) * mm, "radius": 0.25 * mm});
            skCircle(sketch, "E26.6.2.1", {"center": v(-11.85, -21.1) * mm, "radius": 0.25 * mm});
            skCircle(sketch, "E26.6.2.2", {"center": v(-15.85, -26.7) * mm, "radius": 0.25 * mm});
            skCircle(sketch, "E26.6.2.3", {"center": v(-11.85, -26.7) * mm, "radius": 0.25 * mm});
            skCircle(sketch, "E26.6.3.0", {"center": v(-15.85, 27.3) * mm, "radius": 0.25 * mm});
            skCircle(sketch, "E26.6.3.1", {"center": v(-11.85, 27.3) * mm, "radius": 0.25 * mm});
            skCircle(sketch, "E26.6.3.2", {"center": v(-15.85, 21.7) * mm, "radius": 0.25 * mm});
            skCircle(sketch, "E26.6.3.3", {"center": v(-11.85, 21.7) * mm, "radius": 0.25 * mm});
            skCircle(sketch, "E26.6.4.0", {"center": v(-15.85, 75.7) * mm, "radius": 0.25 * mm});
            skCircle(sketch, "E26.6.4.1", {"center": v(-11.85, 75.7) * mm, "radius": 0.25 * mm});
            skCircle(sketch, "E26.6.4.2", {"center": v(-15.85, 70.1) * mm, "radius": 0.25 * mm});
            skCircle(sketch, "E26.6.4.3", {"center": v(-11.85, 70.1) * mm, "radius": 0.25 * mm});
            skCircle(sketch, "E26.6.5.0", {"center": v(-15.85, 124.1) * mm, "radius": 0.25 * mm});
            skCircle(sketch, "E26.6.5.1", {"center": v(-11.85, 124.1) * mm, "radius": 0.25 * mm});
            skCircle(sketch, "E26.6.5.2", {"center": v(-15.85, 118.5) * mm, "radius": 0.25 * mm});
            skCircle(sketch, "E26.6.5.3", {"center": v(-11.85, 118.5) * mm, "radius": 0.25 * mm});
            skCircle(sketch, "E26.7.0.0", {"center": v(12.15, -117.9) * mm, "radius": 0.25 * mm});
            skCircle(sketch, "E26.7.0.1", {"center": v(16.15, -117.9) * mm, "radius": 0.25 * mm});
            skCircle(sketch, "E26.7.0.2", {"center": v(12.15, -123.5) * mm, "radius": 0.25 * mm});
            skCircle(sketch, "E26.7.0.3", {"center": v(16.15, -123.5) * mm, "radius": 0.25 * mm});
            skCircle(sketch, "E26.7.1.0", {"center": v(12.15, -69.5) * mm, "radius": 0.25 * mm});
            skCircle(sketch, "E26.7.1.1", {"center": v(16.15, -69.5) * mm, "radius": 0.25 * mm});
            skCircle(sketch, "E26.7.1.2", {"center": v(12.15, -75.1) * mm, "radius": 0.25 * mm});
            skCircle(sketch, "E26.7.1.3", {"center": v(16.15, -75.1) * mm, "radius": 0.25 * mm});
            skCircle(sketch, "E26.7.2.0", {"center": v(12.15, -21.1) * mm, "radius": 0.25 * mm});
            skCircle(sketch, "E26.7.2.1", {"center": v(16.15, -21.1) * mm, "radius": 0.25 * mm});
            skCircle(sketch, "E26.7.2.2", {"center": v(12.15, -26.7) * mm, "radius": 0.25 * mm});
            skCircle(sketch, "E26.7.2.3", {"center": v(16.15, -26.7) * mm, "radius": 0.25 * mm});
            skCircle(sketch, "E26.7.3.0", {"center": v(12.15, 27.3) * mm, "radius": 0.25 * mm});
            skCircle(sketch, "E26.7.3.1", {"center": v(16.15, 27.3) * mm, "radius": 0.25 * mm});
            skCircle(sketch, "E26.7.3.2", {"center": v(12.15, 21.7) * mm, "radius": 0.25 * mm});
            skCircle(sketch, "E26.7.3.3", {"center": v(16.15, 21.7) * mm, "radius": 0.25 * mm});
            skCircle(sketch, "E26.7.4.0", {"center": v(12.15, 75.7) * mm, "radius": 0.25 * mm});
            skCircle(sketch, "E26.7.4.1", {"center": v(16.15, 75.7) * mm, "radius": 0.25 * mm});
            skCircle(sketch, "E26.7.4.2", {"center": v(12.15, 70.1) * mm, "radius": 0.25 * mm});
            skCircle(sketch, "E26.7.4.3", {"center": v(16.15, 70.1) * mm, "radius": 0.25 * mm});
            skCircle(sketch, "E26.7.5.0", {"center": v(12.15, 124.1) * mm, "radius": 0.25 * mm});
            skCircle(sketch, "E26.7.5.1", {"center": v(16.15, 124.1) * mm, "radius": 0.25 * mm});
            skCircle(sketch, "E26.7.5.2", {"center": v(12.15, 118.5) * mm, "radius": 0.25 * mm});
            skCircle(sketch, "E26.7.5.3", {"center": v(16.15, 118.5) * mm, "radius": 0.25 * mm});
            skCircle(sketch, "E26.8.0.0", {"center": v(40.15, -117.9) * mm, "radius": 0.25 * mm});
            skCircle(sketch, "E26.8.0.1", {"center": v(44.15, -117.9) * mm, "radius": 0.25 * mm});
            skCircle(sketch, "E26.8.0.2", {"center": v(40.15, -123.5) * mm, "radius": 0.25 * mm});
            skCircle(sketch, "E26.8.0.3", {"center": v(44.15, -123.5) * mm, "radius": 0.25 * mm});
            skCircle(sketch, "E26.8.1.0", {"center": v(40.15, -69.5) * mm, "radius": 0.25 * mm});
            skCircle(sketch, "E26.8.1.1", {"center": v(44.15, -69.5) * mm, "radius": 0.25 * mm});
            skCircle(sketch, "E26.8.1.2", {"center": v(40.15, -75.1) * mm, "radius": 0.25 * mm});
            skCircle(sketch, "E26.8.1.3", {"center": v(44.15, -75.1) * mm, "radius": 0.25 * mm});
            skCircle(sketch, "E26.8.2.0", {"center": v(40.15, -21.1) * mm, "radius": 0.25 * mm});
            skCircle(sketch, "E26.8.2.1", {"center": v(44.15, -21.1) * mm, "radius": 0.25 * mm});
            skCircle(sketch, "E26.8.2.2", {"center": v(40.15, -26.7) * mm, "radius": 0.25 * mm});
            skCircle(sketch, "E26.8.2.3", {"center": v(44.15, -26.7) * mm, "radius": 0.25 * mm});
            skCircle(sketch, "E26.8.3.0", {"center": v(40.15, 27.3) * mm, "radius": 0.25 * mm});
            skCircle(sketch, "E26.8.3.1", {"center": v(44.15, 27.3) * mm, "radius": 0.25 * mm});
            skCircle(sketch, "E26.8.3.2", {"center": v(40.15, 21.7) * mm, "radius": 0.25 * mm});
            skCircle(sketch, "E26.8.3.3", {"center": v(44.15, 21.7) * mm, "radius": 0.25 * mm});
            skCircle(sketch, "E26.8.4.0", {"center": v(40.15, 75.7) * mm, "radius": 0.25 * mm});
            skCircle(sketch, "E26.8.4.1", {"center": v(44.15, 75.7) * mm, "radius": 0.25 * mm});
            skCircle(sketch, "E26.8.4.2", {"center": v(40.15, 70.1) * mm, "radius": 0.25 * mm});
            skCircle(sketch, "E26.8.4.3", {"center": v(44.15, 70.1) * mm, "radius": 0.25 * mm});
            skCircle(sketch, "E26.8.5.0", {"center": v(40.15, 124.1) * mm, "radius": 0.25 * mm});
            skCircle(sketch, "E26.8.5.1", {"center": v(44.15, 124.1) * mm, "radius": 0.25 * mm});
            skCircle(sketch, "E26.8.5.2", {"center": v(40.15, 118.5) * mm, "radius": 0.25 * mm});
            skCircle(sketch, "E26.8.5.3", {"center": v(44.15, 118.5) * mm, "radius": 0.25 * mm});
            skCircle(sketch, "E26.9.0.0", {"center": v(68.15, -117.9) * mm, "radius": 0.25 * mm});
            skCircle(sketch, "E26.9.0.1", {"center": v(72.15, -117.9) * mm, "radius": 0.25 * mm});
            skCircle(sketch, "E26.9.0.2", {"center": v(68.15, -123.5) * mm, "radius": 0.25 * mm});
            skCircle(sketch, "E26.9.0.3", {"center": v(72.15, -123.5) * mm, "radius": 0.25 * mm});
            skCircle(sketch, "E26.9.1.0", {"center": v(68.15, -69.5) * mm, "radius": 0.25 * mm});
            skCircle(sketch, "E26.9.1.1", {"center": v(72.15, -69.5) * mm, "radius": 0.25 * mm});
            skCircle(sketch, "E26.9.1.2", {"center": v(68.15, -75.1) * mm, "radius": 0.25 * mm});
            skCircle(sketch, "E26.9.1.3", {"center": v(72.15, -75.1) * mm, "radius": 0.25 * mm});
            skCircle(sketch, "E26.9.2.0", {"center": v(68.15, -21.1) * mm, "radius": 0.25 * mm});
            skCircle(sketch, "E26.9.2.1", {"center": v(72.15, -21.1) * mm, "radius": 0.25 * mm});
            skCircle(sketch, "E26.9.2.2", {"center": v(68.15, -26.7) * mm, "radius": 0.25 * mm});
            skCircle(sketch, "E26.9.2.3", {"center": v(72.15, -26.7) * mm, "radius": 0.25 * mm});
            skCircle(sketch, "E26.9.3.0", {"center": v(68.15, 27.3) * mm, "radius": 0.25 * mm});
            skCircle(sketch, "E26.9.3.1", {"center": v(72.15, 27.3) * mm, "radius": 0.25 * mm});
            skCircle(sketch, "E26.9.3.2", {"center": v(68.15, 21.7) * mm, "radius": 0.25 * mm});
            skCircle(sketch, "E26.9.3.3", {"center": v(72.15, 21.7) * mm, "radius": 0.25 * mm});
            skCircle(sketch, "E26.9.4.0", {"center": v(68.15, 75.7) * mm, "radius": 0.25 * mm});
            skCircle(sketch, "E26.9.4.1", {"center": v(72.15, 75.7) * mm, "radius": 0.25 * mm});
            skCircle(sketch, "E26.9.4.2", {"center": v(68.15, 70.1) * mm, "radius": 0.25 * mm});
            skCircle(sketch, "E26.9.4.3", {"center": v(72.15, 70.1) * mm, "radius": 0.25 * mm});
            skCircle(sketch, "E26.9.5.0", {"center": v(68.15, 124.1) * mm, "radius": 0.25 * mm});
            skCircle(sketch, "E26.9.5.1", {"center": v(72.15, 124.1) * mm, "radius": 0.25 * mm});
            skCircle(sketch, "E26.9.5.2", {"center": v(68.15, 118.5) * mm, "radius": 0.25 * mm});
            skCircle(sketch, "E26.9.5.3", {"center": v(72.15, 118.5) * mm, "radius": 0.25 * mm});
            skCircle(sketch, "E26.10.0.0", {"center": v(96.15, -117.9) * mm, "radius": 0.25 * mm});
            skCircle(sketch, "E26.10.0.1", {"center": v(100.15, -117.9) * mm, "radius": 0.25 * mm});
            skCircle(sketch, "E26.10.0.2", {"center": v(96.15, -123.5) * mm, "radius": 0.25 * mm});
            skCircle(sketch, "E26.10.0.3", {"center": v(100.15, -123.5) * mm, "radius": 0.25 * mm});
            skCircle(sketch, "E26.10.1.0", {"center": v(96.15, -69.5) * mm, "radius": 0.25 * mm});
            skCircle(sketch, "E26.10.1.1", {"center": v(100.15, -69.5) * mm, "radius": 0.25 * mm});
            skCircle(sketch, "E26.10.1.2", {"center": v(96.15, -75.1) * mm, "radius": 0.25 * mm});
            skCircle(sketch, "E26.10.1.3", {"center": v(100.15, -75.1) * mm, "radius": 0.25 * mm});
            skCircle(sketch, "E26.10.2.0", {"center": v(96.15, -21.1) * mm, "radius": 0.25 * mm});
            skCircle(sketch, "E26.10.2.1", {"center": v(100.15, -21.1) * mm, "radius": 0.25 * mm});
            skCircle(sketch, "E26.10.2.2", {"center": v(96.15, -26.7) * mm, "radius": 0.25 * mm});
            skCircle(sketch, "E26.10.2.3", {"center": v(100.15, -26.7) * mm, "radius": 0.25 * mm});
            skCircle(sketch, "E26.10.3.0", {"center": v(96.15, 27.3) * mm, "radius": 0.25 * mm});
            skCircle(sketch, "E26.10.3.1", {"center": v(100.15, 27.3) * mm, "radius": 0.25 * mm});
            skCircle(sketch, "E26.10.3.2", {"center": v(96.15, 21.7) * mm, "radius": 0.25 * mm});
            skCircle(sketch, "E26.10.3.3", {"center": v(100.15, 21.7) * mm, "radius": 0.25 * mm});
            skCircle(sketch, "E26.10.4.0", {"center": v(96.15, 75.7) * mm, "radius": 0.25 * mm});
            skCircle(sketch, "E26.10.4.1", {"center": v(100.15, 75.7) * mm, "radius": 0.25 * mm});
            skCircle(sketch, "E26.10.4.2", {"center": v(96.15, 70.1) * mm, "radius": 0.25 * mm});
            skCircle(sketch, "E26.10.4.3", {"center": v(100.15, 70.1) * mm, "radius": 0.25 * mm});
            skCircle(sketch, "E26.10.5.0", {"center": v(96.15, 124.1) * mm, "radius": 0.25 * mm});
            skCircle(sketch, "E26.10.5.1", {"center": v(100.15, 124.1) * mm, "radius": 0.25 * mm});
            skCircle(sketch, "E26.10.5.2", {"center": v(96.15, 118.5) * mm, "radius": 0.25 * mm});
            skCircle(sketch, "E26.10.5.3", {"center": v(100.15, 118.5) * mm, "radius": 0.25 * mm});
            skCircle(sketch, "E26.11.0.0", {"center": v(124.15, -117.9) * mm, "radius": 0.25 * mm});
            skCircle(sketch, "E26.11.0.1", {"center": v(128.15, -117.9) * mm, "radius": 0.25 * mm});
            skCircle(sketch, "E26.11.0.2", {"center": v(124.15, -123.5) * mm, "radius": 0.25 * mm});
            skCircle(sketch, "E26.11.0.3", {"center": v(128.15, -123.5) * mm, "radius": 0.25 * mm});
            skCircle(sketch, "E26.11.1.0", {"center": v(124.15, -69.5) * mm, "radius": 0.25 * mm});
            skCircle(sketch, "E26.11.1.1", {"center": v(128.15, -69.5) * mm, "radius": 0.25 * mm});
            skCircle(sketch, "E26.11.1.2", {"center": v(124.15, -75.1) * mm, "radius": 0.25 * mm});
            skCircle(sketch, "E26.11.1.3", {"center": v(128.15, -75.1) * mm, "radius": 0.25 * mm});
            skCircle(sketch, "E26.11.2.0", {"center": v(124.15, -21.1) * mm, "radius": 0.25 * mm});
            skCircle(sketch, "E26.11.2.1", {"center": v(128.15, -21.1) * mm, "radius": 0.25 * mm});
            skCircle(sketch, "E26.11.2.2", {"center": v(124.15, -26.7) * mm, "radius": 0.25 * mm});
            skCircle(sketch, "E26.11.2.3", {"center": v(128.15, -26.7) * mm, "radius": 0.25 * mm});
            skCircle(sketch, "E26.11.3.0", {"center": v(124.15, 27.3) * mm, "radius": 0.25 * mm});
            skCircle(sketch, "E26.11.3.1", {"center": v(128.15, 27.3) * mm, "radius": 0.25 * mm});
            skCircle(sketch, "E26.11.3.2", {"center": v(124.15, 21.7) * mm, "radius": 0.25 * mm});
            skCircle(sketch, "E26.11.3.3", {"center": v(128.15, 21.7) * mm, "radius": 0.25 * mm});
            skCircle(sketch, "E26.11.4.0", {"center": v(124.15, 75.7) * mm, "radius": 0.25 * mm});
            skCircle(sketch, "E26.11.4.1", {"center": v(128.15, 75.7) * mm, "radius": 0.25 * mm});
            skCircle(sketch, "E26.11.4.2", {"center": v(124.15, 70.1) * mm, "radius": 0.25 * mm});
            skCircle(sketch, "E26.11.4.3", {"center": v(128.15, 70.1) * mm, "radius": 0.25 * mm});
            skCircle(sketch, "E26.11.5.0", {"center": v(124.15, 124.1) * mm, "radius": 0.25 * mm});
            skCircle(sketch, "E26.11.5.1", {"center": v(128.15, 124.1) * mm, "radius": 0.25 * mm});
            skCircle(sketch, "E26.11.5.2", {"center": v(124.15, 118.5) * mm, "radius": 0.25 * mm});
            skCircle(sketch, "E26.11.5.3", {"center": v(128.15, 118.5) * mm, "radius": 0.25 * mm});
            skCircle(sketch, "E26.12.0.0", {"center": v(152.15, -117.9) * mm, "radius": 0.25 * mm});
            skCircle(sketch, "E26.12.0.1", {"center": v(156.15, -117.9) * mm, "radius": 0.25 * mm});
            skCircle(sketch, "E26.12.0.2", {"center": v(152.15, -123.5) * mm, "radius": 0.25 * mm});
            skCircle(sketch, "E26.12.0.3", {"center": v(156.15, -123.5) * mm, "radius": 0.25 * mm});
            skCircle(sketch, "E26.12.1.0", {"center": v(152.15, -69.5) * mm, "radius": 0.25 * mm});
            skCircle(sketch, "E26.12.1.1", {"center": v(156.15, -69.5) * mm, "radius": 0.25 * mm});
            skCircle(sketch, "E26.12.1.2", {"center": v(152.15, -75.1) * mm, "radius": 0.25 * mm});
            skCircle(sketch, "E26.12.1.3", {"center": v(156.15, -75.1) * mm, "radius": 0.25 * mm});
            skCircle(sketch, "E26.12.2.0", {"center": v(152.15, -21.1) * mm, "radius": 0.25 * mm});
            skCircle(sketch, "E26.12.2.1", {"center": v(156.15, -21.1) * mm, "radius": 0.25 * mm});
            skCircle(sketch, "E26.12.2.2", {"center": v(152.15, -26.7) * mm, "radius": 0.25 * mm});
            skCircle(sketch, "E26.12.2.3", {"center": v(156.15, -26.7) * mm, "radius": 0.25 * mm});
            skCircle(sketch, "E26.12.3.0", {"center": v(152.15, 27.3) * mm, "radius": 0.25 * mm});
            skCircle(sketch, "E26.12.3.1", {"center": v(156.15, 27.3) * mm, "radius": 0.25 * mm});
            skCircle(sketch, "E26.12.3.2", {"center": v(152.15, 21.7) * mm, "radius": 0.25 * mm});
            skCircle(sketch, "E26.12.3.3", {"center": v(156.15, 21.7) * mm, "radius": 0.25 * mm});
            skCircle(sketch, "E26.12.4.0", {"center": v(152.15, 75.7) * mm, "radius": 0.25 * mm});
            skCircle(sketch, "E26.12.4.1", {"center": v(156.15, 75.7) * mm, "radius": 0.25 * mm});
            skCircle(sketch, "E26.12.4.2", {"center": v(152.15, 70.1) * mm, "radius": 0.25 * mm});
            skCircle(sketch, "E26.12.4.3", {"center": v(156.15, 70.1) * mm, "radius": 0.25 * mm});
            skCircle(sketch, "E26.12.5.0", {"center": v(152.15, 124.1) * mm, "radius": 0.25 * mm});
            skCircle(sketch, "E26.12.5.1", {"center": v(156.15, 124.1) * mm, "radius": 0.25 * mm});
            skCircle(sketch, "E26.12.5.2", {"center": v(152.15, 118.5) * mm, "radius": 0.25 * mm});
            skCircle(sketch, "E26.12.5.3", {"center": v(156.15, 118.5) * mm, "radius": 0.25 * mm});
            skCircle(sketch, "E26.13.0.0", {"center": v(180.15, -117.9) * mm, "radius": 0.25 * mm});
            skCircle(sketch, "E26.13.0.1", {"center": v(184.15, -117.9) * mm, "radius": 0.25 * mm});
            skCircle(sketch, "E26.13.0.2", {"center": v(180.15, -123.5) * mm, "radius": 0.25 * mm});
            skCircle(sketch, "E26.13.0.3", {"center": v(184.15, -123.5) * mm, "radius": 0.25 * mm});
            skCircle(sketch, "E26.13.1.0", {"center": v(180.15, -69.5) * mm, "radius": 0.25 * mm});
            skCircle(sketch, "E26.13.1.1", {"center": v(184.15, -69.5) * mm, "radius": 0.25 * mm});
            skCircle(sketch, "E26.13.1.2", {"center": v(180.15, -75.1) * mm, "radius": 0.25 * mm});
            skCircle(sketch, "E26.13.1.3", {"center": v(184.15, -75.1) * mm, "radius": 0.25 * mm});
            skCircle(sketch, "E26.13.2.0", {"center": v(180.15, -21.1) * mm, "radius": 0.25 * mm});
            skCircle(sketch, "E26.13.2.1", {"center": v(184.15, -21.1) * mm, "radius": 0.25 * mm});
            skCircle(sketch, "E26.13.2.2", {"center": v(180.15, -26.7) * mm, "radius": 0.25 * mm});
            skCircle(sketch, "E26.13.2.3", {"center": v(184.15, -26.7) * mm, "radius": 0.25 * mm});
            skCircle(sketch, "E26.13.3.0", {"center": v(180.15, 27.3) * mm, "radius": 0.25 * mm});
            skCircle(sketch, "E26.13.3.1", {"center": v(184.15, 27.3) * mm, "radius": 0.25 * mm});
            skCircle(sketch, "E26.13.3.2", {"center": v(180.15, 21.7) * mm, "radius": 0.25 * mm});
            skCircle(sketch, "E26.13.3.3", {"center": v(184.15, 21.7) * mm, "radius": 0.25 * mm});
            skCircle(sketch, "E26.13.4.0", {"center": v(180.15, 75.7) * mm, "radius": 0.25 * mm});
            skCircle(sketch, "E26.13.4.1", {"center": v(184.15, 75.7) * mm, "radius": 0.25 * mm});
            skCircle(sketch, "E26.13.4.2", {"center": v(180.15, 70.1) * mm, "radius": 0.25 * mm});
            skCircle(sketch, "E26.13.4.3", {"center": v(184.15, 70.1) * mm, "radius": 0.25 * mm});
            skCircle(sketch, "E26.13.5.0", {"center": v(180.15, 124.1) * mm, "radius": 0.25 * mm});
            skCircle(sketch, "E26.13.5.1", {"center": v(184.15, 124.1) * mm, "radius": 0.25 * mm});
            skCircle(sketch, "E26.13.5.2", {"center": v(180.15, 118.5) * mm, "radius": 0.25 * mm});
            skCircle(sketch, "E26.13.5.3", {"center": v(184.15, 118.5) * mm, "radius": 0.25 * mm});
            skLineSegment(sketch, "E26.direction1", {"start": v(-183.85, -123.5) * mm, "end": v(-155.85, -123.5) * mm, "construction": true});
            skLineSegment(sketch, "E26.direction2", {"start": v(-183.85, -123.5) * mm, "end": v(-183.85, -75.1) * mm, "construction": true});
            skSolve(sketch);
        }
        {
            var Q0;
            Q0 = qSketchRegion(id + "F2", true);
            extrude(context, id + "F3", {"entities" : qUnion([Q0]), "depth" : 1 * mm, "offsetDistance" : 25 * mm});
        }
    });
